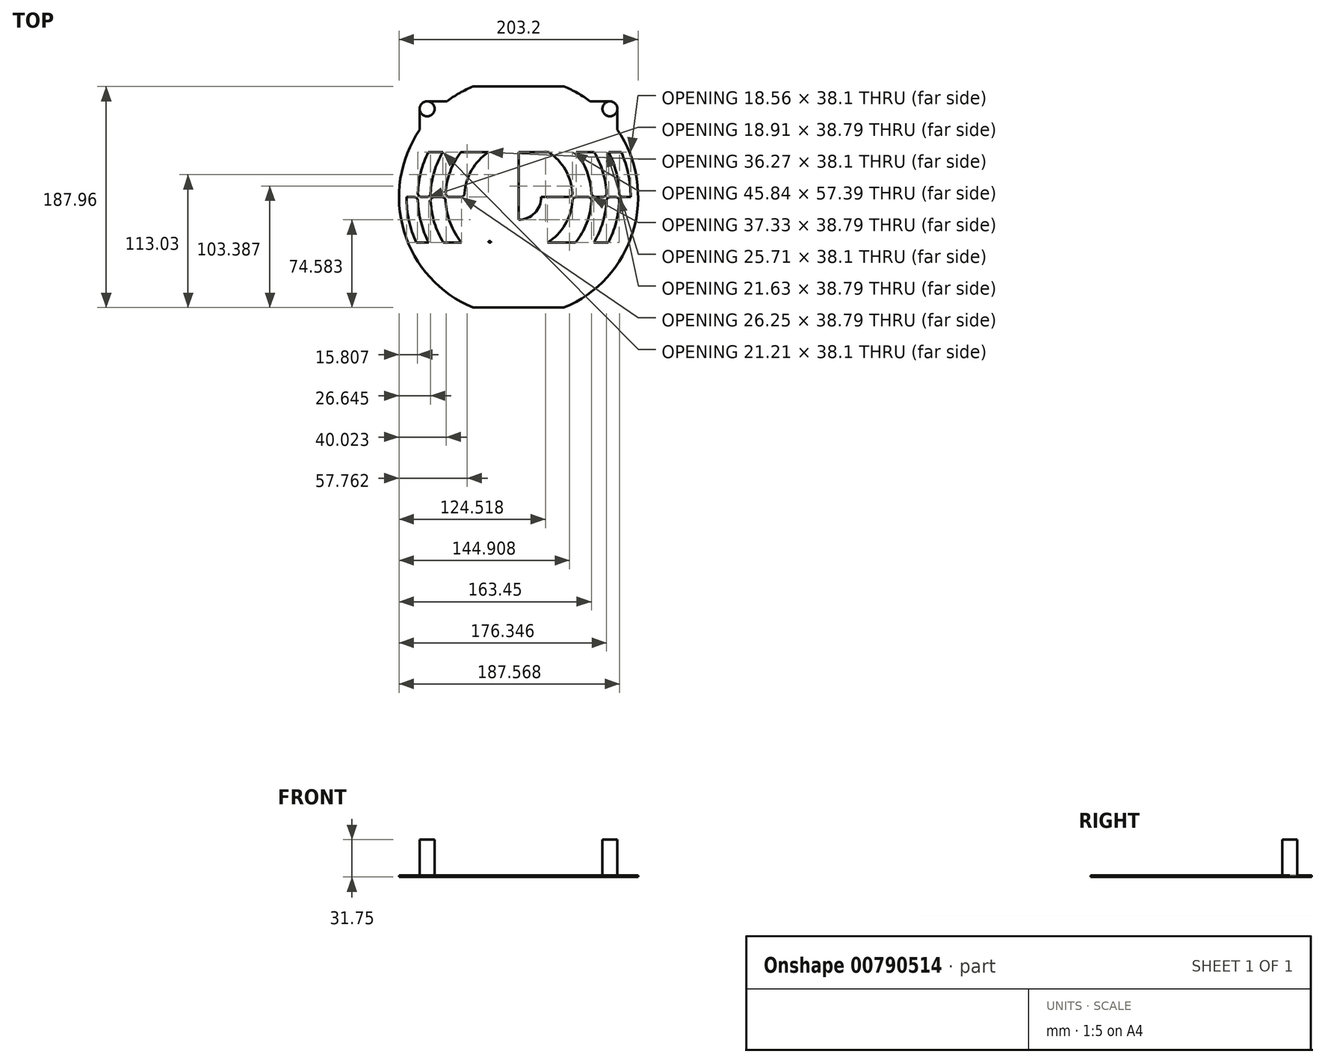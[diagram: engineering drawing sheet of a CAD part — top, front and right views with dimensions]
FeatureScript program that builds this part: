
annotation { "Feature Type Name" : "Feature", "Feature Type Description" : "" }
export const myFeature = defineFeature(function(context is Context, id is Id, definition is map)
    precondition{}
    {
        {
            var Q0;
            Q0=qCreatedBy(makeId("Top.planeOp"),FACE);
            var sketch = newSketch(context, id + "F0", { "sketchPlane" : qUnion([Q0])});
            skCircle(sketch, "E0", {"center": v(0, 0) * mm, "radius": 101.6 * mm});
            skCircle(sketch, "E1", {"center": v(0, 0) * mm, "radius": 45.96 * mm});
            skCircle(sketch, "E2", {"center": v(0, 0) * mm, "radius": 62.07 * mm});
            skCircle(sketch, "E3", {"center": v(0, 0) * mm, "radius": 74.78 * mm});
            skCircle(sketch, "E4", {"center": v(0, 0) * mm, "radius": 85.63 * mm});
            skLineSegment(sketch, "E5", {"start": v(0, 0) * mm, "end": v(0, 38.1) * mm, "construction": true});
            skLineSegment(sketch, "E6", {"start": v(0, 38.1) * mm, "end": v(123.54, 38.1) * mm});
            skLineSegment(sketch, "E7", {"start": v(123.54, 38.1) * mm, "end": v(123.54, 0) * mm});
            skLineSegment(sketch, "E8", {"start": v(123.54, 0) * mm, "end": v(-129.33, 0) * mm});
            skLineSegment(sketch, "E9", {"start": v(-129.33, 0) * mm, "end": v(-129.33, 38.1) * mm});
            skLineSegment(sketch, "E10", {"start": v(-129.33, 38.1) * mm, "end": v(0, 38.1) * mm});
            skLineSegment(sketch, "E11", {"start": v(-129.33, 0) * mm, "end": v(-129.33, -38.8) * mm});
            skLineSegment(sketch, "E12", {"start": v(-129.33, -38.8) * mm, "end": v(123.54, -38.8) * mm});
            skLineSegment(sketch, "E13", {"start": v(123.54, -38.8) * mm, "end": v(123.54, 0) * mm});
            skLineSegment(sketch, "E14", {"start": v(0, 38.1) * mm, "end": v(0, -38.8) * mm});
            skCircle(sketch, "E15", {"center": v(-24.64, -38.8) * mm, "radius": 1.27 * mm});
            skCircle(sketch, "E16", {"center": v(-48.45, -38.8) * mm, "radius": 1.27 * mm});
            skCircle(sketch, "E17", {"center": v(-63.93, -38.8) * mm, "radius": 1.27 * mm});
            skCircle(sketch, "E18", {"center": v(-76.34, -38.8) * mm, "radius": 1.27 * mm});
            skCircle(sketch, "E19", {"center": v(-76.69, 38.1) * mm, "radius": 1.27 * mm});
            skCircle(sketch, "E20", {"center": v(-63.93, 38.1) * mm, "radius": 1.27 * mm});
            skCircle(sketch, "E21", {"center": v(-49, 38.1) * mm, "radius": 1.27 * mm});
            skCircle(sketch, "E22", {"center": v(-25.7, 38.1) * mm, "radius": 1.27 * mm});
            skCircle(sketch, "E23", {"center": v(25.7, 38.1) * mm, "radius": 1.27 * mm});
            skCircle(sketch, "E24", {"center": v(49, 38.1) * mm, "radius": 1.27 * mm});
            skCircle(sketch, "E25", {"center": v(64.35, 38.1) * mm, "radius": 1.27 * mm});
            skCircle(sketch, "E26", {"center": v(76.69, 38.1) * mm, "radius": 1.27 * mm});
            skCircle(sketch, "E27", {"center": v(76.34, -38.8) * mm, "radius": 1.27 * mm});
            skCircle(sketch, "E28", {"center": v(63.93, -38.8) * mm, "radius": 1.27 * mm});
            skCircle(sketch, "E29", {"center": v(48.45, -38.8) * mm, "radius": 1.27 * mm});
            skCircle(sketch, "E30", {"center": v(24.64, -38.8) * mm, "radius": 1.27 * mm});
            skCircle(sketch, "E31", {"center": v(85.63, 0) * mm, "radius": 1.27 * mm});
            skCircle(sketch, "E32", {"center": v(74.78, 0) * mm, "radius": 1.27 * mm});
            skCircle(sketch, "E33", {"center": v(62.07, 0) * mm, "radius": 1.27 * mm});
            skCircle(sketch, "E34", {"center": v(45.96, 0) * mm, "radius": 1.27 * mm});
            skCircle(sketch, "E35", {"center": v(-45.96, 0) * mm, "radius": 1.27 * mm});
            skCircle(sketch, "E36", {"center": v(-62.07, 0) * mm, "radius": 1.27 * mm});
            skCircle(sketch, "E37", {"center": v(-74.78, 0) * mm, "radius": 1.27 * mm});
            skCircle(sketch, "E38", {"center": v(-85.63, 0) * mm, "radius": 1.27 * mm});
            skCircle(sketch, "E39", {"center": v(0, 0) * mm, "radius": 19.29 * mm});
            skCircle(sketch, "E40", {"center": v(-77.66, 74.98) * mm, "radius": 6.35 * mm});
            skCircle(sketch, "E41", {"center": v(77.66, 74.98) * mm, "radius": 6.35 * mm});
            skLineSegment(sketch, "E42", {"start": v(77.66, 74.98) * mm, "end": v(77.66, 81.33) * mm, "construction": true});
            skLineSegment(sketch, "E43", {"start": v(77.66, 74.98) * mm, "end": v(84, 74.98) * mm, "construction": true});
            skLineSegment(sketch, "E44", {"start": v(-77.66, 74.98) * mm, "end": v(-77.66, 81.33) * mm, "construction": true});
            skLineSegment(sketch, "E45", {"start": v(-77.66, 74.98) * mm, "end": v(-84, 74.98) * mm, "construction": true});
            skLineSegment(sketch, "E46", {"start": v(77.66, 81.33) * mm, "end": v(60.9, 81.33) * mm});
            skLineSegment(sketch, "E47", {"start": v(84, 74.98) * mm, "end": v(84, 57.14) * mm});
            skLineSegment(sketch, "E48", {"start": v(-77.66, 81.33) * mm, "end": v(-60.9, 81.33) * mm});
            skLineSegment(sketch, "E49", {"start": v(-84, 74.98) * mm, "end": v(-84, 57.14) * mm});
            skSolve(sketch);
        }
        {
            var Q0;
            {var subQ3=sQuery(id+"F0.wireOp",EDGE,"E22");var subQ5=sQuery(id+"F0.wireOp",EDGE,"E1");var subQ6=makeQuery(id+"F0.imprint","INTERSECT",VERTEX,{"disambiguationData":[OD(1.0)],"derivedFrom":[subQ5,subQ3]});Q0=makeQuery(id+"F0.imprint","IMPRINT",FACE,{"disambiguationData":[TD([[makeQuery(id+"F0.imprint","IMPRINT",EDGE,{"disambiguationData":[TD([[subQ6,-1.0]])],"derivedFrom":subQ5}),1.0]])]});}
            var Q1;
            {var subQ3=sQuery(id+"F0.wireOp",EDGE,"E30");var subQ11=sQuery(id+"F0.wireOp",EDGE,"E1");var subQ12=makeQuery(id+"F0.imprint","INTERSECT",VERTEX,{"disambiguationData":[OD(1.0)],"derivedFrom":[subQ11,subQ3]});Q1=makeQuery(id+"F0.imprint","IMPRINT",FACE,{"disambiguationData":[TD([[makeQuery(id+"F0.imprint","IMPRINT",EDGE,{"disambiguationData":[TD([[subQ12,-1.0]])],"derivedFrom":subQ11}),1.0]])]});}
            var Q2;
            {var subQ3=sQuery(id+"F0.wireOp",EDGE,"E34");var subQ13=sQuery(id+"F0.wireOp",EDGE,"E1");var subQ14=makeQuery(id+"F0.imprint","INTERSECT",VERTEX,{"disambiguationData":[OD(0.0)],"derivedFrom":[subQ13,subQ3]});Q2=makeQuery(id+"F0.imprint","IMPRINT",FACE,{"disambiguationData":[TD([[makeQuery(id+"F0.imprint","IMPRINT",EDGE,{"disambiguationData":[TD([[subQ14,-1.0]])],"derivedFrom":subQ13}),-1.0]])]});}
            var Q3;
            {var subQ0=sQuery(id+"F0.wireOp",EDGE,"E29");var subQ8=sQuery(id+"F0.wireOp",EDGE,"E2");var subQ15=makeQuery(id+"F0.imprint","INTERSECT",VERTEX,{"disambiguationData":[OD(1.0)],"derivedFrom":[subQ8,subQ0]});Q3=makeQuery(id+"F0.imprint","IMPRINT",FACE,{"disambiguationData":[TD([[makeQuery(id+"F0.imprint","IMPRINT",EDGE,{"disambiguationData":[TD([[subQ15,-1.0]])],"derivedFrom":subQ8}),-1.0]])]});}
            var Q4;
            {var subQ3=sQuery(id+"F0.wireOp",EDGE,"E32");var subQ10=sQuery(id+"F0.wireOp",EDGE,"E3");var subQ11=makeQuery(id+"F0.imprint","INTERSECT",VERTEX,{"disambiguationData":[OD(0.0)],"derivedFrom":[subQ10,subQ3]});Q4=makeQuery(id+"F0.imprint","IMPRINT",FACE,{"disambiguationData":[TD([[makeQuery(id+"F0.imprint","IMPRINT",EDGE,{"disambiguationData":[TD([[subQ11,-1.0]])],"derivedFrom":subQ10}),-1.0]])]});}
            var Q5;
            {var subQ1=sQuery(id+"F0.wireOp",EDGE,"E0");var subQ9=sQuery(id+"F0.wireOp",EDGE,"E12");var subQ10=makeQuery(id+"F0.imprint","INTERSECT",VERTEX,{"disambiguationData":[OD(1.0)],"derivedFrom":[subQ1,subQ9]});Q5=makeQuery(id+"F0.imprint","IMPRINT",FACE,{"disambiguationData":[TD([[makeQuery(id+"F0.imprint","IMPRINT",EDGE,{"disambiguationData":[TD([[subQ10,-1.0]])],"derivedFrom":subQ1}),1.0]])]});}
            var Q6;
            {var subQ0=sQuery(id+"F0.wireOp",EDGE,"E35");var subQ13=sQuery(id+"F0.wireOp",EDGE,"E1");var subQ14=makeQuery(id+"F0.imprint","INTERSECT",VERTEX,{"disambiguationData":[OD(1.0)],"derivedFrom":[subQ13,subQ0]});Q6=makeQuery(id+"F0.imprint","IMPRINT",FACE,{"disambiguationData":[TD([[makeQuery(id+"F0.imprint","IMPRINT",EDGE,{"disambiguationData":[TD([[subQ14,-1.0]])],"derivedFrom":subQ13}),-1.0]])]});}
            var Q7;
            {var subQ11=sQuery(id+"F0.wireOp",EDGE,"E21");var subQ13=sQuery(id+"F0.wireOp",EDGE,"E2");var subQ14=makeQuery(id+"F0.imprint","INTERSECT",VERTEX,{"disambiguationData":[OD(1.0)],"derivedFrom":[subQ13,subQ11]});Q7=makeQuery(id+"F0.imprint","IMPRINT",FACE,{"disambiguationData":[TD([[makeQuery(id+"F0.imprint","IMPRINT",EDGE,{"disambiguationData":[TD([[subQ14,-1.0]])],"derivedFrom":subQ13}),-1.0]])]});}
            var Q8;
            {var subQ5=sQuery(id+"F0.wireOp",EDGE,"E37");var subQ10=sQuery(id+"F0.wireOp",EDGE,"E3");var subQ11=makeQuery(id+"F0.imprint","INTERSECT",VERTEX,{"disambiguationData":[OD(1.0)],"derivedFrom":[subQ10,subQ5]});Q8=makeQuery(id+"F0.imprint","IMPRINT",FACE,{"disambiguationData":[TD([[makeQuery(id+"F0.imprint","IMPRINT",EDGE,{"disambiguationData":[TD([[subQ11,-1.0]])],"derivedFrom":subQ10}),-1.0]])]});}
            var Q9;
            {var subQ0=sQuery(id+"F0.wireOp",EDGE,"E10");var subQ1=sQuery(id+"F0.wireOp",EDGE,"E0");var subQ2=makeQuery(id+"F0.imprint","INTERSECT",VERTEX,{"derivedFrom":[subQ1,subQ0]});Q9=makeQuery(id+"F0.imprint","IMPRINT",FACE,{"disambiguationData":[TD([[makeQuery(id+"F0.imprint","IMPRINT",EDGE,{"disambiguationData":[TD([[subQ2,-1.0]])],"derivedFrom":subQ1}),1.0]])]});}
            var Q10;
            {var subQ0=sQuery(id+"F0.wireOp",EDGE,"E38");var subQ1=sQuery(id+"F0.wireOp",EDGE,"E4");var subQ2=makeQuery(id+"F0.imprint","INTERSECT",VERTEX,{"disambiguationData":[OD(0.0)],"derivedFrom":[subQ1,subQ0]});Q10=makeQuery(id+"F0.imprint","IMPRINT",FACE,{"disambiguationData":[TD([[makeQuery(id+"F0.imprint","IMPRINT",EDGE,{"disambiguationData":[TD([[subQ2,-1.0]])],"derivedFrom":subQ1}),1.0]])]});}
            var Q11;
            {var subQ0=sQuery(id+"F0.wireOp",EDGE,"E8");var subQ1=sQuery(id+"F0.wireOp",EDGE,"E4");var subQ2=makeQuery(id+"F0.imprint","INTERSECT",VERTEX,{"disambiguationData":[OD(1.0)],"derivedFrom":[subQ1,subQ0]});Q11=makeQuery(id+"F0.imprint","IMPRINT",FACE,{"disambiguationData":[TD([[makeQuery(id+"F0.imprint","IMPRINT",EDGE,{"disambiguationData":[TD([[subQ2,-1.0]])],"derivedFrom":subQ1}),1.0]])]});}
            var Q12;
            {var subQ0=sQuery(id+"F0.wireOp",EDGE,"E8");var subQ1=sQuery(id+"F0.wireOp",EDGE,"E4");var subQ2=makeQuery(id+"F0.imprint","INTERSECT",VERTEX,{"disambiguationData":[OD(1.0)],"derivedFrom":[subQ1,subQ0]});Q12=makeQuery(id+"F0.imprint","IMPRINT",FACE,{"disambiguationData":[TD([[makeQuery(id+"F0.imprint","IMPRINT",EDGE,{"disambiguationData":[TD([[subQ2,-1.0]])],"derivedFrom":subQ1}),-1.0]])]});}
            var Q13;
            {var subQ0=sQuery(id+"F0.wireOp",EDGE,"E38");var subQ1=sQuery(id+"F0.wireOp",EDGE,"E4");var subQ2=makeQuery(id+"F0.imprint","INTERSECT",VERTEX,{"disambiguationData":[OD(0.0)],"derivedFrom":[subQ1,subQ0]});Q13=makeQuery(id+"F0.imprint","IMPRINT",FACE,{"disambiguationData":[TD([[makeQuery(id+"F0.imprint","IMPRINT",EDGE,{"disambiguationData":[TD([[subQ2,-1.0]])],"derivedFrom":subQ1}),-1.0]])]});}
            var Q14;
            {var subQ0=sQuery(id+"F0.wireOp",EDGE,"E37");var subQ1=sQuery(id+"F0.wireOp",EDGE,"E3");var subQ2=makeQuery(id+"F0.imprint","INTERSECT",VERTEX,{"disambiguationData":[OD(0.0)],"derivedFrom":[subQ1,subQ0]});Q14=makeQuery(id+"F0.imprint","IMPRINT",FACE,{"disambiguationData":[TD([[makeQuery(id+"F0.imprint","IMPRINT",EDGE,{"disambiguationData":[TD([[subQ2,-1.0]])],"derivedFrom":subQ1}),-1.0]])]});}
            var Q15;
            {var subQ0=sQuery(id+"F0.wireOp",EDGE,"E37");var subQ1=sQuery(id+"F0.wireOp",EDGE,"E3");var subQ2=makeQuery(id+"F0.imprint","INTERSECT",VERTEX,{"disambiguationData":[OD(0.0)],"derivedFrom":[subQ1,subQ0]});Q15=makeQuery(id+"F0.imprint","IMPRINT",FACE,{"disambiguationData":[TD([[makeQuery(id+"F0.imprint","IMPRINT",EDGE,{"disambiguationData":[TD([[subQ2,-1.0]])],"derivedFrom":subQ1}),1.0]])]});}
            var Q16;
            {var subQ0=sQuery(id+"F0.wireOp",EDGE,"E8");var subQ1=sQuery(id+"F0.wireOp",EDGE,"E3");var subQ2=makeQuery(id+"F0.imprint","INTERSECT",VERTEX,{"disambiguationData":[OD(1.0)],"derivedFrom":[subQ1,subQ0]});Q16=makeQuery(id+"F0.imprint","IMPRINT",FACE,{"disambiguationData":[TD([[makeQuery(id+"F0.imprint","IMPRINT",EDGE,{"disambiguationData":[TD([[subQ2,-1.0]])],"derivedFrom":subQ1}),1.0]])]});}
            var Q17;
            {var subQ0=sQuery(id+"F0.wireOp",EDGE,"E8");var subQ1=sQuery(id+"F0.wireOp",EDGE,"E3");var subQ2=makeQuery(id+"F0.imprint","INTERSECT",VERTEX,{"disambiguationData":[OD(1.0)],"derivedFrom":[subQ1,subQ0]});Q17=makeQuery(id+"F0.imprint","IMPRINT",FACE,{"disambiguationData":[TD([[makeQuery(id+"F0.imprint","IMPRINT",EDGE,{"disambiguationData":[TD([[subQ2,-1.0]])],"derivedFrom":subQ1}),-1.0]])]});}
            var Q18;
            {var subQ0=sQuery(id+"F0.wireOp",EDGE,"E36");var subQ1=sQuery(id+"F0.wireOp",EDGE,"E2");var subQ2=makeQuery(id+"F0.imprint","INTERSECT",VERTEX,{"disambiguationData":[OD(0.0)],"derivedFrom":[subQ1,subQ0]});Q18=makeQuery(id+"F0.imprint","IMPRINT",FACE,{"disambiguationData":[TD([[makeQuery(id+"F0.imprint","IMPRINT",EDGE,{"disambiguationData":[TD([[subQ2,-1.0]])],"derivedFrom":subQ1}),-1.0]])]});}
            var Q19;
            {var subQ0=sQuery(id+"F0.wireOp",EDGE,"E36");var subQ1=sQuery(id+"F0.wireOp",EDGE,"E2");var subQ2=makeQuery(id+"F0.imprint","INTERSECT",VERTEX,{"disambiguationData":[OD(0.0)],"derivedFrom":[subQ1,subQ0]});Q19=makeQuery(id+"F0.imprint","IMPRINT",FACE,{"disambiguationData":[TD([[makeQuery(id+"F0.imprint","IMPRINT",EDGE,{"disambiguationData":[TD([[subQ2,-1.0]])],"derivedFrom":subQ1}),1.0]])]});}
            var Q20;
            {var subQ0=sQuery(id+"F0.wireOp",EDGE,"E8");var subQ1=sQuery(id+"F0.wireOp",EDGE,"E2");var subQ2=makeQuery(id+"F0.imprint","INTERSECT",VERTEX,{"disambiguationData":[OD(1.0)],"derivedFrom":[subQ1,subQ0]});Q20=makeQuery(id+"F0.imprint","IMPRINT",FACE,{"disambiguationData":[TD([[makeQuery(id+"F0.imprint","IMPRINT",EDGE,{"disambiguationData":[TD([[subQ2,-1.0]])],"derivedFrom":subQ1}),1.0]])]});}
            var Q21;
            {var subQ0=sQuery(id+"F0.wireOp",EDGE,"E8");var subQ1=sQuery(id+"F0.wireOp",EDGE,"E2");var subQ2=makeQuery(id+"F0.imprint","INTERSECT",VERTEX,{"disambiguationData":[OD(1.0)],"derivedFrom":[subQ1,subQ0]});Q21=makeQuery(id+"F0.imprint","IMPRINT",FACE,{"disambiguationData":[TD([[makeQuery(id+"F0.imprint","IMPRINT",EDGE,{"disambiguationData":[TD([[subQ2,-1.0]])],"derivedFrom":subQ1}),-1.0]])]});}
            var Q22;
            {var subQ0=sQuery(id+"F0.wireOp",EDGE,"E35");var subQ1=sQuery(id+"F0.wireOp",EDGE,"E1");var subQ2=makeQuery(id+"F0.imprint","INTERSECT",VERTEX,{"disambiguationData":[OD(0.0)],"derivedFrom":[subQ1,subQ0]});Q22=makeQuery(id+"F0.imprint","IMPRINT",FACE,{"disambiguationData":[TD([[makeQuery(id+"F0.imprint","IMPRINT",EDGE,{"disambiguationData":[TD([[subQ2,-1.0]])],"derivedFrom":subQ1}),-1.0]])]});}
            var Q23;
            {var subQ0=sQuery(id+"F0.wireOp",EDGE,"E35");var subQ1=sQuery(id+"F0.wireOp",EDGE,"E1");var subQ2=makeQuery(id+"F0.imprint","INTERSECT",VERTEX,{"disambiguationData":[OD(0.0)],"derivedFrom":[subQ1,subQ0]});Q23=makeQuery(id+"F0.imprint","IMPRINT",FACE,{"disambiguationData":[TD([[makeQuery(id+"F0.imprint","IMPRINT",EDGE,{"disambiguationData":[TD([[subQ2,-1.0]])],"derivedFrom":subQ1}),1.0]])]});}
            var Q24;
            {var subQ0=sQuery(id+"F0.wireOp",EDGE,"E8");var subQ1=sQuery(id+"F0.wireOp",EDGE,"E1");var subQ2=makeQuery(id+"F0.imprint","INTERSECT",VERTEX,{"disambiguationData":[OD(1.0)],"derivedFrom":[subQ1,subQ0]});Q24=makeQuery(id+"F0.imprint","IMPRINT",FACE,{"disambiguationData":[TD([[makeQuery(id+"F0.imprint","IMPRINT",EDGE,{"disambiguationData":[TD([[subQ2,-1.0]])],"derivedFrom":subQ1}),1.0]])]});}
            var Q25;
            {var subQ0=sQuery(id+"F0.wireOp",EDGE,"E8");var subQ1=sQuery(id+"F0.wireOp",EDGE,"E1");var subQ2=makeQuery(id+"F0.imprint","INTERSECT",VERTEX,{"disambiguationData":[OD(1.0)],"derivedFrom":[subQ1,subQ0]});Q25=makeQuery(id+"F0.imprint","IMPRINT",FACE,{"disambiguationData":[TD([[makeQuery(id+"F0.imprint","IMPRINT",EDGE,{"disambiguationData":[TD([[subQ2,-1.0]])],"derivedFrom":subQ1}),-1.0]])]});}
            var Q26;
            {var subQ0=sQuery(id+"F0.wireOp",EDGE,"E8");var subQ1=sQuery(id+"F0.wireOp",EDGE,"E1");var subQ2=makeQuery(id+"F0.imprint","INTERSECT",VERTEX,{"disambiguationData":[OD(0.0)],"derivedFrom":[subQ1,subQ0]});Q26=makeQuery(id+"F0.imprint","IMPRINT",FACE,{"disambiguationData":[TD([[makeQuery(id+"F0.imprint","IMPRINT",EDGE,{"disambiguationData":[TD([[subQ2,1.0]])],"derivedFrom":subQ1}),-1.0]])]});}
            var Q27;
            {var subQ0=sQuery(id+"F0.wireOp",EDGE,"E34");var subQ1=sQuery(id+"F0.wireOp",EDGE,"E1");var subQ2=makeQuery(id+"F0.imprint","INTERSECT",VERTEX,{"disambiguationData":[OD(0.0)],"derivedFrom":[subQ1,subQ0]});Q27=makeQuery(id+"F0.imprint","IMPRINT",FACE,{"disambiguationData":[TD([[makeQuery(id+"F0.imprint","IMPRINT",EDGE,{"disambiguationData":[TD([[subQ2,1.0]])],"derivedFrom":subQ1}),-1.0]])]});}
            var Q28;
            {var subQ0=sQuery(id+"F0.wireOp",EDGE,"E34");var subQ1=sQuery(id+"F0.wireOp",EDGE,"E1");var subQ2=makeQuery(id+"F0.imprint","INTERSECT",VERTEX,{"disambiguationData":[OD(0.0)],"derivedFrom":[subQ1,subQ0]});Q28=makeQuery(id+"F0.imprint","IMPRINT",FACE,{"disambiguationData":[TD([[makeQuery(id+"F0.imprint","IMPRINT",EDGE,{"disambiguationData":[TD([[subQ2,1.0]])],"derivedFrom":subQ1}),1.0]])]});}
            var Q29;
            {var subQ0=sQuery(id+"F0.wireOp",EDGE,"E33");var subQ1=sQuery(id+"F0.wireOp",EDGE,"E2");var subQ2=makeQuery(id+"F0.imprint","INTERSECT",VERTEX,{"disambiguationData":[OD(0.0)],"derivedFrom":[subQ1,subQ0]});Q29=makeQuery(id+"F0.imprint","IMPRINT",FACE,{"disambiguationData":[TD([[makeQuery(id+"F0.imprint","IMPRINT",EDGE,{"disambiguationData":[TD([[subQ2,1.0]])],"derivedFrom":subQ1}),1.0]])]});}
            var Q30;
            {var subQ0=sQuery(id+"F0.wireOp",EDGE,"E33");var subQ1=sQuery(id+"F0.wireOp",EDGE,"E2");var subQ2=makeQuery(id+"F0.imprint","INTERSECT",VERTEX,{"disambiguationData":[OD(0.0)],"derivedFrom":[subQ1,subQ0]});Q30=makeQuery(id+"F0.imprint","IMPRINT",FACE,{"disambiguationData":[TD([[makeQuery(id+"F0.imprint","IMPRINT",EDGE,{"disambiguationData":[TD([[subQ2,1.0]])],"derivedFrom":subQ1}),-1.0]])]});}
            var Q31;
            {var subQ0=sQuery(id+"F0.wireOp",EDGE,"E8");var subQ1=sQuery(id+"F0.wireOp",EDGE,"E2");var subQ2=makeQuery(id+"F0.imprint","INTERSECT",VERTEX,{"disambiguationData":[OD(0.0)],"derivedFrom":[subQ1,subQ0]});Q31=makeQuery(id+"F0.imprint","IMPRINT",FACE,{"disambiguationData":[TD([[makeQuery(id+"F0.imprint","IMPRINT",EDGE,{"disambiguationData":[TD([[subQ2,1.0]])],"derivedFrom":subQ1}),-1.0]])]});}
            var Q32;
            {var subQ0=sQuery(id+"F0.wireOp",EDGE,"E8");var subQ1=sQuery(id+"F0.wireOp",EDGE,"E2");var subQ2=makeQuery(id+"F0.imprint","INTERSECT",VERTEX,{"disambiguationData":[OD(0.0)],"derivedFrom":[subQ1,subQ0]});Q32=makeQuery(id+"F0.imprint","IMPRINT",FACE,{"disambiguationData":[TD([[makeQuery(id+"F0.imprint","IMPRINT",EDGE,{"disambiguationData":[TD([[subQ2,1.0]])],"derivedFrom":subQ1}),1.0]])]});}
            var Q33;
            {var subQ0=sQuery(id+"F0.wireOp",EDGE,"E32");var subQ1=sQuery(id+"F0.wireOp",EDGE,"E3");var subQ2=makeQuery(id+"F0.imprint","INTERSECT",VERTEX,{"disambiguationData":[OD(0.0)],"derivedFrom":[subQ1,subQ0]});Q33=makeQuery(id+"F0.imprint","IMPRINT",FACE,{"disambiguationData":[TD([[makeQuery(id+"F0.imprint","IMPRINT",EDGE,{"disambiguationData":[TD([[subQ2,1.0]])],"derivedFrom":subQ1}),1.0]])]});}
            var Q34;
            {var subQ0=sQuery(id+"F0.wireOp",EDGE,"E8");var subQ1=sQuery(id+"F0.wireOp",EDGE,"E3");var subQ2=makeQuery(id+"F0.imprint","INTERSECT",VERTEX,{"disambiguationData":[OD(0.0)],"derivedFrom":[subQ1,subQ0]});Q34=makeQuery(id+"F0.imprint","IMPRINT",FACE,{"disambiguationData":[TD([[makeQuery(id+"F0.imprint","IMPRINT",EDGE,{"disambiguationData":[TD([[subQ2,1.0]])],"derivedFrom":subQ1}),1.0]])]});}
            var Q35;
            {var subQ0=sQuery(id+"F0.wireOp",EDGE,"E8");var subQ1=sQuery(id+"F0.wireOp",EDGE,"E3");var subQ2=makeQuery(id+"F0.imprint","INTERSECT",VERTEX,{"disambiguationData":[OD(0.0)],"derivedFrom":[subQ1,subQ0]});Q35=makeQuery(id+"F0.imprint","IMPRINT",FACE,{"disambiguationData":[TD([[makeQuery(id+"F0.imprint","IMPRINT",EDGE,{"disambiguationData":[TD([[subQ2,1.0]])],"derivedFrom":subQ1}),-1.0]])]});}
            var Q36;
            {var subQ0=sQuery(id+"F0.wireOp",EDGE,"E32");var subQ1=sQuery(id+"F0.wireOp",EDGE,"E3");var subQ2=makeQuery(id+"F0.imprint","INTERSECT",VERTEX,{"disambiguationData":[OD(0.0)],"derivedFrom":[subQ1,subQ0]});Q36=makeQuery(id+"F0.imprint","IMPRINT",FACE,{"disambiguationData":[TD([[makeQuery(id+"F0.imprint","IMPRINT",EDGE,{"disambiguationData":[TD([[subQ2,1.0]])],"derivedFrom":subQ1}),-1.0]])]});}
            var Q37;
            {var subQ0=sQuery(id+"F0.wireOp",EDGE,"E31");var subQ1=sQuery(id+"F0.wireOp",EDGE,"E4");var subQ2=makeQuery(id+"F0.imprint","INTERSECT",VERTEX,{"disambiguationData":[OD(0.0)],"derivedFrom":[subQ1,subQ0]});Q37=makeQuery(id+"F0.imprint","IMPRINT",FACE,{"disambiguationData":[TD([[makeQuery(id+"F0.imprint","IMPRINT",EDGE,{"disambiguationData":[TD([[subQ2,1.0]])],"derivedFrom":subQ1}),1.0]])]});}
            var Q38;
            {var subQ0=sQuery(id+"F0.wireOp",EDGE,"E31");var subQ1=sQuery(id+"F0.wireOp",EDGE,"E4");var subQ2=makeQuery(id+"F0.imprint","INTERSECT",VERTEX,{"disambiguationData":[OD(0.0)],"derivedFrom":[subQ1,subQ0]});Q38=makeQuery(id+"F0.imprint","IMPRINT",FACE,{"disambiguationData":[TD([[makeQuery(id+"F0.imprint","IMPRINT",EDGE,{"disambiguationData":[TD([[subQ2,1.0]])],"derivedFrom":subQ1}),-1.0]])]});}
            var Q39;
            {var subQ0=sQuery(id+"F0.wireOp",EDGE,"E8");var subQ1=sQuery(id+"F0.wireOp",EDGE,"E4");var subQ2=makeQuery(id+"F0.imprint","INTERSECT",VERTEX,{"disambiguationData":[OD(0.0)],"derivedFrom":[subQ1,subQ0]});Q39=makeQuery(id+"F0.imprint","IMPRINT",FACE,{"disambiguationData":[TD([[makeQuery(id+"F0.imprint","IMPRINT",EDGE,{"disambiguationData":[TD([[subQ2,1.0]])],"derivedFrom":subQ1}),-1.0]])]});}
            var Q40;
            {var subQ0=sQuery(id+"F0.wireOp",EDGE,"E8");var subQ1=sQuery(id+"F0.wireOp",EDGE,"E4");var subQ2=makeQuery(id+"F0.imprint","INTERSECT",VERTEX,{"disambiguationData":[OD(0.0)],"derivedFrom":[subQ1,subQ0]});Q40=makeQuery(id+"F0.imprint","IMPRINT",FACE,{"disambiguationData":[TD([[makeQuery(id+"F0.imprint","IMPRINT",EDGE,{"disambiguationData":[TD([[subQ2,1.0]])],"derivedFrom":subQ1}),1.0]])]});}
            var Q41;
            {var subQ0=sQuery(id+"F0.wireOp",EDGE,"E14");var subQ1=sQuery(id+"F0.wireOp",EDGE,"E8");var subQ2=makeQuery(id+"F0.imprint","INTERSECT",VERTEX,{"derivedFrom":[subQ1,subQ0]});Q41=makeQuery(id+"F0.imprint","IMPRINT",FACE,{"disambiguationData":[TD([[makeQuery(id+"F0.imprint","IMPRINT",EDGE,{"disambiguationData":[TD([[subQ2,-1.0]])],"derivedFrom":subQ1}),-1.0]])]});}
            var Q42;
            {var subQ0=sQuery(id+"F0.wireOp",EDGE,"E39");var subQ1=sQuery(id+"F0.wireOp",EDGE,"E8");var subQ2=makeQuery(id+"F0.imprint","INTERSECT",VERTEX,{"disambiguationData":[OD(0.0)],"derivedFrom":[subQ1,subQ0]});Q42=makeQuery(id+"F0.imprint","IMPRINT",FACE,{"disambiguationData":[TD([[makeQuery(id+"F0.imprint","IMPRINT",EDGE,{"disambiguationData":[TD([[subQ2,-1.0]])],"derivedFrom":subQ1}),-1.0]])]});}
            var Q43;
            {var subQ0=sQuery(id+"F0.wireOp",EDGE,"E39");var subQ1=sQuery(id+"F0.wireOp",EDGE,"E8");var subQ2=makeQuery(id+"F0.imprint","INTERSECT",VERTEX,{"disambiguationData":[OD(0.0)],"derivedFrom":[subQ1,subQ0]});Q43=makeQuery(id+"F0.imprint","IMPRINT",FACE,{"disambiguationData":[TD([[makeQuery(id+"F0.imprint","IMPRINT",EDGE,{"disambiguationData":[TD([[subQ2,-1.0]])],"derivedFrom":subQ1}),1.0]])]});}
            var Q44;
            {var subQ0=sQuery(id+"F0.wireOp",EDGE,"E14");var subQ1=sQuery(id+"F0.wireOp",EDGE,"E8");var subQ2=makeQuery(id+"F0.imprint","INTERSECT",VERTEX,{"derivedFrom":[subQ1,subQ0]});Q44=makeQuery(id+"F0.imprint","IMPRINT",FACE,{"disambiguationData":[TD([[makeQuery(id+"F0.imprint","IMPRINT",EDGE,{"disambiguationData":[TD([[subQ2,-1.0]])],"derivedFrom":subQ1}),1.0]])]});}
            var Q45;
            {var subQ0=sQuery(id+"F0.wireOp",EDGE,"E8");var subQ1=sQuery(id+"F0.wireOp",EDGE,"E1");var subQ2=makeQuery(id+"F0.imprint","INTERSECT",VERTEX,{"disambiguationData":[OD(0.0)],"derivedFrom":[subQ1,subQ0]});Q45=makeQuery(id+"F0.imprint","IMPRINT",FACE,{"disambiguationData":[TD([[makeQuery(id+"F0.imprint","IMPRINT",EDGE,{"disambiguationData":[TD([[subQ2,1.0]])],"derivedFrom":subQ1}),1.0]])]});}
            var Q46;
            {var subQ1=sQuery(id+"F0.wireOp",EDGE,"E0");var subQ5=sQuery(id+"F0.wireOp",EDGE,"E6");var subQ6=makeQuery(id+"F0.imprint","INTERSECT",VERTEX,{"derivedFrom":[subQ1,subQ5]});Q46=makeQuery(id+"F0.imprint","IMPRINT",FACE,{"disambiguationData":[TD([[makeQuery(id+"F0.imprint","IMPRINT",EDGE,{"disambiguationData":[TD([[subQ6,-1.0]])],"derivedFrom":subQ1}),1.0]])]});}
            var Q47;
            {var subQ5=sQuery(id+"F0.wireOp",EDGE,"E25");var subQ13=sQuery(id+"F0.wireOp",EDGE,"E3");var subQ14=makeQuery(id+"F0.imprint","INTERSECT",VERTEX,{"disambiguationData":[OD(1.0)],"derivedFrom":[subQ13,subQ5]});Q47=makeQuery(id+"F0.imprint","IMPRINT",FACE,{"disambiguationData":[TD([[makeQuery(id+"F0.imprint","IMPRINT",EDGE,{"disambiguationData":[TD([[subQ14,-1.0]])],"derivedFrom":subQ13}),-1.0]])]});}
            var Q48;
            {var subQ0=sQuery(id+"F0.wireOp",EDGE,"E24");var subQ10=sQuery(id+"F0.wireOp",EDGE,"E2");var subQ12=makeQuery(id+"F0.imprint","INTERSECT",VERTEX,{"disambiguationData":[OD(1.0)],"derivedFrom":[subQ10,subQ0]});Q48=makeQuery(id+"F0.imprint","IMPRINT",FACE,{"disambiguationData":[TD([[makeQuery(id+"F0.imprint","IMPRINT",EDGE,{"disambiguationData":[TD([[subQ12,-1.0]])],"derivedFrom":subQ10}),-1.0]])]});}
            var Q49;
            {var subQ5=sQuery(id+"F0.wireOp",EDGE,"E23");var subQ13=sQuery(id+"F0.wireOp",EDGE,"E1");var subQ14=makeQuery(id+"F0.imprint","INTERSECT",VERTEX,{"disambiguationData":[OD(1.0)],"derivedFrom":[subQ13,subQ5]});Q49=makeQuery(id+"F0.imprint","IMPRINT",FACE,{"disambiguationData":[TD([[makeQuery(id+"F0.imprint","IMPRINT",EDGE,{"disambiguationData":[TD([[subQ14,-1.0]])],"derivedFrom":subQ13}),-1.0]])]});}
            var Q50;
            {var subQ5=sQuery(id+"F0.wireOp",EDGE,"E23");var subQ7=sQuery(id+"F0.wireOp",EDGE,"E1");var subQ9=makeQuery(id+"F0.imprint","INTERSECT",VERTEX,{"disambiguationData":[OD(1.0)],"derivedFrom":[subQ7,subQ5]});Q50=makeQuery(id+"F0.imprint","IMPRINT",FACE,{"disambiguationData":[TD([[makeQuery(id+"F0.imprint","IMPRINT",EDGE,{"disambiguationData":[TD([[subQ9,-1.0]])],"derivedFrom":subQ7}),1.0]])]});}
            var Q51;
            {var subQ0=sQuery(id+"F0.wireOp",EDGE,"E15");var subQ1=sQuery(id+"F0.wireOp",EDGE,"E1");var subQ2=makeQuery(id+"F0.imprint","INTERSECT",VERTEX,{"disambiguationData":[OD(1.0)],"derivedFrom":[subQ1,subQ0]});Q51=makeQuery(id+"F0.imprint","IMPRINT",FACE,{"disambiguationData":[TD([[makeQuery(id+"F0.imprint","IMPRINT",EDGE,{"disambiguationData":[TD([[subQ2,-1.0]])],"derivedFrom":subQ1}),1.0]])]});}
            var Q52;
            {var subQ7=sQuery(id+"F0.wireOp",EDGE,"E16");var subQ12=sQuery(id+"F0.wireOp",EDGE,"E2");var subQ14=makeQuery(id+"F0.imprint","INTERSECT",VERTEX,{"disambiguationData":[OD(1.0)],"derivedFrom":[subQ12,subQ7]});Q52=makeQuery(id+"F0.imprint","IMPRINT",FACE,{"disambiguationData":[TD([[makeQuery(id+"F0.imprint","IMPRINT",EDGE,{"disambiguationData":[TD([[subQ14,-1.0]])],"derivedFrom":subQ12}),-1.0]])]});}
            var Q53;
            {var subQ7=sQuery(id+"F0.wireOp",EDGE,"E17");var subQ9=sQuery(id+"F0.wireOp",EDGE,"E3");var subQ10=makeQuery(id+"F0.imprint","INTERSECT",VERTEX,{"disambiguationData":[OD(1.0)],"derivedFrom":[subQ9,subQ7]});Q53=makeQuery(id+"F0.imprint","IMPRINT",FACE,{"disambiguationData":[TD([[makeQuery(id+"F0.imprint","IMPRINT",EDGE,{"disambiguationData":[TD([[subQ10,-1.0]])],"derivedFrom":subQ9}),-1.0]])]});}
            var Q54;
            {var subQ0=sQuery(id+"F0.wireOp",EDGE,"E12");var subQ1=sQuery(id+"F0.wireOp",EDGE,"E0");var subQ5=makeQuery(id+"F0.imprint","INTERSECT",VERTEX,{"disambiguationData":[OD(0.0)],"derivedFrom":[subQ1,subQ0]});Q54=makeQuery(id+"F0.imprint","IMPRINT",FACE,{"disambiguationData":[TD([[makeQuery(id+"F0.imprint","IMPRINT",EDGE,{"disambiguationData":[TD([[subQ5,-1.0]])],"derivedFrom":subQ1}),1.0]])]});}
            var Q55;
            {var subQ0=sQuery(id+"F0.wireOp",EDGE,"E23");var subQ1=sQuery(id+"F0.wireOp",EDGE,"E1");var subQ2=makeQuery(id+"F0.imprint","INTERSECT",VERTEX,{"disambiguationData":[OD(0.0)],"derivedFrom":[subQ1,subQ0]});Q55=makeQuery(id+"F0.imprint","IMPRINT",FACE,{"disambiguationData":[TD([[makeQuery(id+"F0.imprint","IMPRINT",EDGE,{"disambiguationData":[TD([[subQ2,-1.0]])],"derivedFrom":subQ1}),-1.0]])]});}
            var Q56;
            {var subQ0=sQuery(id+"F0.wireOp",EDGE,"E6");var subQ1=sQuery(id+"F0.wireOp",EDGE,"E1");var subQ2=makeQuery(id+"F0.imprint","INTERSECT",VERTEX,{"derivedFrom":[subQ1,subQ0]});Q56=makeQuery(id+"F0.imprint","IMPRINT",FACE,{"disambiguationData":[TD([[makeQuery(id+"F0.imprint","IMPRINT",EDGE,{"disambiguationData":[TD([[subQ2,-1.0]])],"derivedFrom":subQ1}),1.0]])]});}
            var Q57;
            {var subQ0=sQuery(id+"F0.wireOp",EDGE,"E22");var subQ1=sQuery(id+"F0.wireOp",EDGE,"E1");var subQ2=makeQuery(id+"F0.imprint","INTERSECT",VERTEX,{"disambiguationData":[OD(0.0)],"derivedFrom":[subQ1,subQ0]});Q57=makeQuery(id+"F0.imprint","IMPRINT",FACE,{"disambiguationData":[TD([[makeQuery(id+"F0.imprint","IMPRINT",EDGE,{"disambiguationData":[TD([[subQ2,-1.0]])],"derivedFrom":subQ1}),-1.0]])]});}
            var Q58;
            {var subQ0=sQuery(id+"F0.wireOp",EDGE,"E22");var subQ1=sQuery(id+"F0.wireOp",EDGE,"E1");var subQ2=makeQuery(id+"F0.imprint","INTERSECT",VERTEX,{"disambiguationData":[OD(0.0)],"derivedFrom":[subQ1,subQ0]});Q58=makeQuery(id+"F0.imprint","IMPRINT",FACE,{"disambiguationData":[TD([[makeQuery(id+"F0.imprint","IMPRINT",EDGE,{"disambiguationData":[TD([[subQ2,-1.0]])],"derivedFrom":subQ1}),1.0]])]});}
            var Q59;
            {var subQ0=sQuery(id+"F0.wireOp",EDGE,"E15");var subQ1=sQuery(id+"F0.wireOp",EDGE,"E1");var subQ2=makeQuery(id+"F0.imprint","INTERSECT",VERTEX,{"disambiguationData":[OD(0.0)],"derivedFrom":[subQ1,subQ0]});Q59=makeQuery(id+"F0.imprint","IMPRINT",FACE,{"disambiguationData":[TD([[makeQuery(id+"F0.imprint","IMPRINT",EDGE,{"disambiguationData":[TD([[subQ2,-1.0]])],"derivedFrom":subQ1}),-1.0]])]});}
            var Q60;
            {var subQ0=sQuery(id+"F0.wireOp",EDGE,"E12");var subQ1=sQuery(id+"F0.wireOp",EDGE,"E1");var subQ2=makeQuery(id+"F0.imprint","INTERSECT",VERTEX,{"disambiguationData":[OD(0.0)],"derivedFrom":[subQ1,subQ0]});Q60=makeQuery(id+"F0.imprint","IMPRINT",FACE,{"disambiguationData":[TD([[makeQuery(id+"F0.imprint","IMPRINT",EDGE,{"disambiguationData":[TD([[subQ2,-1.0]])],"derivedFrom":subQ1}),1.0]])]});}
            var Q61;
            {var subQ0=sQuery(id+"F0.wireOp",EDGE,"E30");var subQ1=sQuery(id+"F0.wireOp",EDGE,"E1");var subQ2=makeQuery(id+"F0.imprint","INTERSECT",VERTEX,{"disambiguationData":[OD(0.0)],"derivedFrom":[subQ1,subQ0]});Q61=makeQuery(id+"F0.imprint","IMPRINT",FACE,{"disambiguationData":[TD([[makeQuery(id+"F0.imprint","IMPRINT",EDGE,{"disambiguationData":[TD([[subQ2,-1.0]])],"derivedFrom":subQ1}),1.0]])]});}
            var Q62;
            {var subQ0=sQuery(id+"F0.wireOp",EDGE,"E30");var subQ1=sQuery(id+"F0.wireOp",EDGE,"E1");var subQ2=makeQuery(id+"F0.imprint","INTERSECT",VERTEX,{"disambiguationData":[OD(0.0)],"derivedFrom":[subQ1,subQ0]});Q62=makeQuery(id+"F0.imprint","IMPRINT",FACE,{"disambiguationData":[TD([[makeQuery(id+"F0.imprint","IMPRINT",EDGE,{"disambiguationData":[TD([[subQ2,-1.0]])],"derivedFrom":subQ1}),-1.0]])]});}
            var Q63;
            {var subQ0=sQuery(id+"F0.wireOp",EDGE,"E12");var subQ1=sQuery(id+"F0.wireOp",EDGE,"E1");var subQ2=makeQuery(id+"F0.imprint","INTERSECT",VERTEX,{"disambiguationData":[OD(1.0)],"derivedFrom":[subQ1,subQ0]});Q63=makeQuery(id+"F0.imprint","IMPRINT",FACE,{"disambiguationData":[TD([[makeQuery(id+"F0.imprint","IMPRINT",EDGE,{"disambiguationData":[TD([[subQ2,-1.0]])],"derivedFrom":subQ1}),1.0]])]});}
            var Q64;
            {var subQ9=sQuery(id+"F0.wireOp",EDGE,"E1");var subQ12=sQuery(id+"F0.wireOp",EDGE,"E15");var subQ14=makeQuery(id+"F0.imprint","INTERSECT",VERTEX,{"disambiguationData":[OD(1.0)],"derivedFrom":[subQ9,subQ12]});Q64=makeQuery(id+"F0.imprint","IMPRINT",FACE,{"disambiguationData":[TD([[makeQuery(id+"F0.imprint","IMPRINT",EDGE,{"disambiguationData":[TD([[subQ14,-1.0]])],"derivedFrom":subQ9}),-1.0]])]});}
            var Q65;
            {var subQ0=sQuery(id+"F0.wireOp",EDGE,"E12");var subQ1=sQuery(id+"F0.wireOp",EDGE,"E1");var subQ2=makeQuery(id+"F0.imprint","INTERSECT",VERTEX,{"disambiguationData":[OD(0.0)],"derivedFrom":[subQ1,subQ0]});Q65=makeQuery(id+"F0.imprint","IMPRINT",FACE,{"disambiguationData":[TD([[makeQuery(id+"F0.imprint","IMPRINT",EDGE,{"disambiguationData":[TD([[subQ2,-1.0]])],"derivedFrom":subQ1}),-1.0]])]});}
            var Q66;
            {var subQ0=sQuery(id+"F0.wireOp",EDGE,"E29");var subQ1=sQuery(id+"F0.wireOp",EDGE,"E2");var subQ2=makeQuery(id+"F0.imprint","INTERSECT",VERTEX,{"disambiguationData":[OD(0.0)],"derivedFrom":[subQ1,subQ0]});Q66=makeQuery(id+"F0.imprint","IMPRINT",FACE,{"disambiguationData":[TD([[makeQuery(id+"F0.imprint","IMPRINT",EDGE,{"disambiguationData":[TD([[subQ2,-1.0]])],"derivedFrom":subQ1}),1.0]])]});}
            var Q67;
            {var subQ0=sQuery(id+"F0.wireOp",EDGE,"E29");var subQ1=sQuery(id+"F0.wireOp",EDGE,"E2");var subQ2=makeQuery(id+"F0.imprint","INTERSECT",VERTEX,{"disambiguationData":[OD(0.0)],"derivedFrom":[subQ1,subQ0]});Q67=makeQuery(id+"F0.imprint","IMPRINT",FACE,{"disambiguationData":[TD([[makeQuery(id+"F0.imprint","IMPRINT",EDGE,{"disambiguationData":[TD([[subQ2,-1.0]])],"derivedFrom":subQ1}),-1.0]])]});}
            var Q68;
            {var subQ0=sQuery(id+"F0.wireOp",EDGE,"E12");var subQ1=sQuery(id+"F0.wireOp",EDGE,"E2");var subQ2=makeQuery(id+"F0.imprint","INTERSECT",VERTEX,{"disambiguationData":[OD(1.0)],"derivedFrom":[subQ1,subQ0]});Q68=makeQuery(id+"F0.imprint","IMPRINT",FACE,{"disambiguationData":[TD([[makeQuery(id+"F0.imprint","IMPRINT",EDGE,{"disambiguationData":[TD([[subQ2,-1.0]])],"derivedFrom":subQ1}),-1.0]])]});}
            var Q69;
            {var subQ0=sQuery(id+"F0.wireOp",EDGE,"E28");var subQ1=sQuery(id+"F0.wireOp",EDGE,"E3");var subQ2=makeQuery(id+"F0.imprint","INTERSECT",VERTEX,{"disambiguationData":[OD(0.0)],"derivedFrom":[subQ1,subQ0]});Q69=makeQuery(id+"F0.imprint","IMPRINT",FACE,{"disambiguationData":[TD([[makeQuery(id+"F0.imprint","IMPRINT",EDGE,{"disambiguationData":[TD([[subQ2,-1.0]])],"derivedFrom":subQ1}),1.0]])]});}
            var Q70;
            {var subQ0=sQuery(id+"F0.wireOp",EDGE,"E12");var subQ1=sQuery(id+"F0.wireOp",EDGE,"E3");var subQ2=makeQuery(id+"F0.imprint","INTERSECT",VERTEX,{"disambiguationData":[OD(1.0)],"derivedFrom":[subQ1,subQ0]});Q70=makeQuery(id+"F0.imprint","IMPRINT",FACE,{"disambiguationData":[TD([[makeQuery(id+"F0.imprint","IMPRINT",EDGE,{"disambiguationData":[TD([[subQ2,-1.0]])],"derivedFrom":subQ1}),1.0]])]});}
            var Q71;
            {var subQ0=sQuery(id+"F0.wireOp",EDGE,"E28");var subQ1=sQuery(id+"F0.wireOp",EDGE,"E3");var subQ2=makeQuery(id+"F0.imprint","INTERSECT",VERTEX,{"disambiguationData":[OD(0.0)],"derivedFrom":[subQ1,subQ0]});Q71=makeQuery(id+"F0.imprint","IMPRINT",FACE,{"disambiguationData":[TD([[makeQuery(id+"F0.imprint","IMPRINT",EDGE,{"disambiguationData":[TD([[subQ2,-1.0]])],"derivedFrom":subQ1}),-1.0]])]});}
            var Q72;
            {var subQ0=sQuery(id+"F0.wireOp",EDGE,"E27");var subQ1=sQuery(id+"F0.wireOp",EDGE,"E4");var subQ2=makeQuery(id+"F0.imprint","INTERSECT",VERTEX,{"disambiguationData":[OD(0.0)],"derivedFrom":[subQ1,subQ0]});Q72=makeQuery(id+"F0.imprint","IMPRINT",FACE,{"disambiguationData":[TD([[makeQuery(id+"F0.imprint","IMPRINT",EDGE,{"disambiguationData":[TD([[subQ2,-1.0]])],"derivedFrom":subQ1}),1.0]])]});}
            var Q73;
            {var subQ0=sQuery(id+"F0.wireOp",EDGE,"E27");var subQ1=sQuery(id+"F0.wireOp",EDGE,"E4");var subQ2=makeQuery(id+"F0.imprint","INTERSECT",VERTEX,{"disambiguationData":[OD(0.0)],"derivedFrom":[subQ1,subQ0]});Q73=makeQuery(id+"F0.imprint","IMPRINT",FACE,{"disambiguationData":[TD([[makeQuery(id+"F0.imprint","IMPRINT",EDGE,{"disambiguationData":[TD([[subQ2,-1.0]])],"derivedFrom":subQ1}),-1.0]])]});}
            var Q74;
            {var subQ0=sQuery(id+"F0.wireOp",EDGE,"E12");var subQ1=sQuery(id+"F0.wireOp",EDGE,"E4");var subQ2=makeQuery(id+"F0.imprint","INTERSECT",VERTEX,{"disambiguationData":[OD(1.0)],"derivedFrom":[subQ1,subQ0]});Q74=makeQuery(id+"F0.imprint","IMPRINT",FACE,{"disambiguationData":[TD([[makeQuery(id+"F0.imprint","IMPRINT",EDGE,{"disambiguationData":[TD([[subQ2,-1.0]])],"derivedFrom":subQ1}),-1.0]])]});}
            var Q75;
            {var subQ0=sQuery(id+"F0.wireOp",EDGE,"E6");var subQ1=sQuery(id+"F0.wireOp",EDGE,"E4");var subQ2=makeQuery(id+"F0.imprint","INTERSECT",VERTEX,{"derivedFrom":[subQ1,subQ0]});Q75=makeQuery(id+"F0.imprint","IMPRINT",FACE,{"disambiguationData":[TD([[makeQuery(id+"F0.imprint","IMPRINT",EDGE,{"disambiguationData":[TD([[subQ2,-1.0]])],"derivedFrom":subQ1}),-1.0]])]});}
            var Q76;
            {var subQ0=sQuery(id+"F0.wireOp",EDGE,"E6");var subQ1=sQuery(id+"F0.wireOp",EDGE,"E4");var subQ2=makeQuery(id+"F0.imprint","INTERSECT",VERTEX,{"derivedFrom":[subQ1,subQ0]});Q76=makeQuery(id+"F0.imprint","IMPRINT",FACE,{"disambiguationData":[TD([[makeQuery(id+"F0.imprint","IMPRINT",EDGE,{"disambiguationData":[TD([[subQ2,-1.0]])],"derivedFrom":subQ1}),1.0]])]});}
            var Q77;
            {var subQ0=sQuery(id+"F0.wireOp",EDGE,"E26");var subQ1=sQuery(id+"F0.wireOp",EDGE,"E4");var subQ2=makeQuery(id+"F0.imprint","INTERSECT",VERTEX,{"disambiguationData":[OD(0.0)],"derivedFrom":[subQ1,subQ0]});Q77=makeQuery(id+"F0.imprint","IMPRINT",FACE,{"disambiguationData":[TD([[makeQuery(id+"F0.imprint","IMPRINT",EDGE,{"disambiguationData":[TD([[subQ2,-1.0]])],"derivedFrom":subQ1}),1.0]])]});}
            var Q78;
            {var subQ0=sQuery(id+"F0.wireOp",EDGE,"E25");var subQ1=sQuery(id+"F0.wireOp",EDGE,"E3");var subQ2=makeQuery(id+"F0.imprint","INTERSECT",VERTEX,{"disambiguationData":[OD(0.0)],"derivedFrom":[subQ1,subQ0]});Q78=makeQuery(id+"F0.imprint","IMPRINT",FACE,{"disambiguationData":[TD([[makeQuery(id+"F0.imprint","IMPRINT",EDGE,{"disambiguationData":[TD([[subQ2,-1.0]])],"derivedFrom":subQ1}),-1.0]])]});}
            var Q79;
            {var subQ0=sQuery(id+"F0.wireOp",EDGE,"E6");var subQ1=sQuery(id+"F0.wireOp",EDGE,"E3");var subQ2=makeQuery(id+"F0.imprint","INTERSECT",VERTEX,{"derivedFrom":[subQ1,subQ0]});Q79=makeQuery(id+"F0.imprint","IMPRINT",FACE,{"disambiguationData":[TD([[makeQuery(id+"F0.imprint","IMPRINT",EDGE,{"disambiguationData":[TD([[subQ2,-1.0]])],"derivedFrom":subQ1}),-1.0]])]});}
            var Q80;
            {var subQ0=sQuery(id+"F0.wireOp",EDGE,"E6");var subQ1=sQuery(id+"F0.wireOp",EDGE,"E3");var subQ2=makeQuery(id+"F0.imprint","INTERSECT",VERTEX,{"derivedFrom":[subQ1,subQ0]});Q80=makeQuery(id+"F0.imprint","IMPRINT",FACE,{"disambiguationData":[TD([[makeQuery(id+"F0.imprint","IMPRINT",EDGE,{"disambiguationData":[TD([[subQ2,-1.0]])],"derivedFrom":subQ1}),1.0]])]});}
            var Q81;
            {var subQ0=sQuery(id+"F0.wireOp",EDGE,"E24");var subQ1=sQuery(id+"F0.wireOp",EDGE,"E2");var subQ2=makeQuery(id+"F0.imprint","INTERSECT",VERTEX,{"disambiguationData":[OD(0.0)],"derivedFrom":[subQ1,subQ0]});Q81=makeQuery(id+"F0.imprint","IMPRINT",FACE,{"disambiguationData":[TD([[makeQuery(id+"F0.imprint","IMPRINT",EDGE,{"disambiguationData":[TD([[subQ2,-1.0]])],"derivedFrom":subQ1}),1.0]])]});}
            var Q82;
            {var subQ0=sQuery(id+"F0.wireOp",EDGE,"E6");var subQ1=sQuery(id+"F0.wireOp",EDGE,"E2");var subQ2=makeQuery(id+"F0.imprint","INTERSECT",VERTEX,{"derivedFrom":[subQ1,subQ0]});Q82=makeQuery(id+"F0.imprint","IMPRINT",FACE,{"disambiguationData":[TD([[makeQuery(id+"F0.imprint","IMPRINT",EDGE,{"disambiguationData":[TD([[subQ2,-1.0]])],"derivedFrom":subQ1}),1.0]])]});}
            var Q83;
            {var subQ0=sQuery(id+"F0.wireOp",EDGE,"E6");var subQ1=sQuery(id+"F0.wireOp",EDGE,"E2");var subQ2=makeQuery(id+"F0.imprint","INTERSECT",VERTEX,{"derivedFrom":[subQ1,subQ0]});Q83=makeQuery(id+"F0.imprint","IMPRINT",FACE,{"disambiguationData":[TD([[makeQuery(id+"F0.imprint","IMPRINT",EDGE,{"disambiguationData":[TD([[subQ2,-1.0]])],"derivedFrom":subQ1}),-1.0]])]});}
            var Q84;
            {var subQ0=sQuery(id+"F0.wireOp",EDGE,"E6");var subQ1=sQuery(id+"F0.wireOp",EDGE,"E1");var subQ2=makeQuery(id+"F0.imprint","INTERSECT",VERTEX,{"derivedFrom":[subQ1,subQ0]});Q84=makeQuery(id+"F0.imprint","IMPRINT",FACE,{"disambiguationData":[TD([[makeQuery(id+"F0.imprint","IMPRINT",EDGE,{"disambiguationData":[TD([[subQ2,-1.0]])],"derivedFrom":subQ1}),-1.0]])]});}
            var Q85;
            {var subQ0=sQuery(id+"F0.wireOp",EDGE,"E10");var subQ1=sQuery(id+"F0.wireOp",EDGE,"E1");var subQ2=makeQuery(id+"F0.imprint","INTERSECT",VERTEX,{"derivedFrom":[subQ1,subQ0]});Q85=makeQuery(id+"F0.imprint","IMPRINT",FACE,{"disambiguationData":[TD([[makeQuery(id+"F0.imprint","IMPRINT",EDGE,{"disambiguationData":[TD([[subQ2,-1.0]])],"derivedFrom":subQ1}),1.0]])]});}
            var Q86;
            {var subQ0=sQuery(id+"F0.wireOp",EDGE,"E21");var subQ1=sQuery(id+"F0.wireOp",EDGE,"E2");var subQ2=makeQuery(id+"F0.imprint","INTERSECT",VERTEX,{"disambiguationData":[OD(0.0)],"derivedFrom":[subQ1,subQ0]});Q86=makeQuery(id+"F0.imprint","IMPRINT",FACE,{"disambiguationData":[TD([[makeQuery(id+"F0.imprint","IMPRINT",EDGE,{"disambiguationData":[TD([[subQ2,-1.0]])],"derivedFrom":subQ1}),-1.0]])]});}
            var Q87;
            {var subQ0=sQuery(id+"F0.wireOp",EDGE,"E21");var subQ1=sQuery(id+"F0.wireOp",EDGE,"E2");var subQ2=makeQuery(id+"F0.imprint","INTERSECT",VERTEX,{"disambiguationData":[OD(0.0)],"derivedFrom":[subQ1,subQ0]});Q87=makeQuery(id+"F0.imprint","IMPRINT",FACE,{"disambiguationData":[TD([[makeQuery(id+"F0.imprint","IMPRINT",EDGE,{"disambiguationData":[TD([[subQ2,-1.0]])],"derivedFrom":subQ1}),1.0]])]});}
            var Q88;
            {var subQ0=sQuery(id+"F0.wireOp",EDGE,"E10");var subQ1=sQuery(id+"F0.wireOp",EDGE,"E2");var subQ2=makeQuery(id+"F0.imprint","INTERSECT",VERTEX,{"derivedFrom":[subQ1,subQ0]});Q88=makeQuery(id+"F0.imprint","IMPRINT",FACE,{"disambiguationData":[TD([[makeQuery(id+"F0.imprint","IMPRINT",EDGE,{"disambiguationData":[TD([[subQ2,-1.0]])],"derivedFrom":subQ1}),-1.0]])]});}
            var Q89;
            {var subQ0=sQuery(id+"F0.wireOp",EDGE,"E20");var subQ1=sQuery(id+"F0.wireOp",EDGE,"E3");var subQ2=makeQuery(id+"F0.imprint","INTERSECT",VERTEX,{"disambiguationData":[OD(0.0)],"derivedFrom":[subQ1,subQ0]});Q89=makeQuery(id+"F0.imprint","IMPRINT",FACE,{"disambiguationData":[TD([[makeQuery(id+"F0.imprint","IMPRINT",EDGE,{"disambiguationData":[TD([[subQ2,-1.0]])],"derivedFrom":subQ1}),-1.0]])]});}
            var Q90;
            {var subQ0=sQuery(id+"F0.wireOp",EDGE,"E20");var subQ1=sQuery(id+"F0.wireOp",EDGE,"E3");var subQ2=makeQuery(id+"F0.imprint","INTERSECT",VERTEX,{"disambiguationData":[OD(0.0)],"derivedFrom":[subQ1,subQ0]});Q90=makeQuery(id+"F0.imprint","IMPRINT",FACE,{"disambiguationData":[TD([[makeQuery(id+"F0.imprint","IMPRINT",EDGE,{"disambiguationData":[TD([[subQ2,-1.0]])],"derivedFrom":subQ1}),1.0]])]});}
            var Q91;
            {var subQ0=sQuery(id+"F0.wireOp",EDGE,"E10");var subQ1=sQuery(id+"F0.wireOp",EDGE,"E3");var subQ2=makeQuery(id+"F0.imprint","INTERSECT",VERTEX,{"derivedFrom":[subQ1,subQ0]});Q91=makeQuery(id+"F0.imprint","IMPRINT",FACE,{"disambiguationData":[TD([[makeQuery(id+"F0.imprint","IMPRINT",EDGE,{"disambiguationData":[TD([[subQ2,-1.0]])],"derivedFrom":subQ1}),1.0]])]});}
            var Q92;
            {var subQ0=sQuery(id+"F0.wireOp",EDGE,"E10");var subQ1=sQuery(id+"F0.wireOp",EDGE,"E4");var subQ2=makeQuery(id+"F0.imprint","INTERSECT",VERTEX,{"derivedFrom":[subQ1,subQ0]});Q92=makeQuery(id+"F0.imprint","IMPRINT",FACE,{"disambiguationData":[TD([[makeQuery(id+"F0.imprint","IMPRINT",EDGE,{"disambiguationData":[TD([[subQ2,-1.0]])],"derivedFrom":subQ1}),-1.0]])]});}
            var Q93;
            {var subQ0=sQuery(id+"F0.wireOp",EDGE,"E19");var subQ1=sQuery(id+"F0.wireOp",EDGE,"E4");var subQ2=makeQuery(id+"F0.imprint","INTERSECT",VERTEX,{"disambiguationData":[OD(0.0)],"derivedFrom":[subQ1,subQ0]});Q93=makeQuery(id+"F0.imprint","IMPRINT",FACE,{"disambiguationData":[TD([[makeQuery(id+"F0.imprint","IMPRINT",EDGE,{"disambiguationData":[TD([[subQ2,-1.0]])],"derivedFrom":subQ1}),1.0]])]});}
            var Q94;
            {var subQ0=sQuery(id+"F0.wireOp",EDGE,"E12");var subQ1=sQuery(id+"F0.wireOp",EDGE,"E2");var subQ2=makeQuery(id+"F0.imprint","INTERSECT",VERTEX,{"disambiguationData":[OD(0.0)],"derivedFrom":[subQ1,subQ0]});Q94=makeQuery(id+"F0.imprint","IMPRINT",FACE,{"disambiguationData":[TD([[makeQuery(id+"F0.imprint","IMPRINT",EDGE,{"disambiguationData":[TD([[subQ2,-1.0]])],"derivedFrom":subQ1}),-1.0]])]});}
            var Q95;
            {var subQ0=sQuery(id+"F0.wireOp",EDGE,"E12");var subQ1=sQuery(id+"F0.wireOp",EDGE,"E2");var subQ2=makeQuery(id+"F0.imprint","INTERSECT",VERTEX,{"disambiguationData":[OD(0.0)],"derivedFrom":[subQ1,subQ0]});Q95=makeQuery(id+"F0.imprint","IMPRINT",FACE,{"disambiguationData":[TD([[makeQuery(id+"F0.imprint","IMPRINT",EDGE,{"disambiguationData":[TD([[subQ2,-1.0]])],"derivedFrom":subQ1}),1.0]])]});}
            var Q96;
            {var subQ0=sQuery(id+"F0.wireOp",EDGE,"E16");var subQ1=sQuery(id+"F0.wireOp",EDGE,"E2");var subQ2=makeQuery(id+"F0.imprint","INTERSECT",VERTEX,{"disambiguationData":[OD(0.0)],"derivedFrom":[subQ1,subQ0]});Q96=makeQuery(id+"F0.imprint","IMPRINT",FACE,{"disambiguationData":[TD([[makeQuery(id+"F0.imprint","IMPRINT",EDGE,{"disambiguationData":[TD([[subQ2,-1.0]])],"derivedFrom":subQ1}),1.0]])]});}
            var Q97;
            {var subQ0=sQuery(id+"F0.wireOp",EDGE,"E17");var subQ1=sQuery(id+"F0.wireOp",EDGE,"E3");var subQ2=makeQuery(id+"F0.imprint","INTERSECT",VERTEX,{"disambiguationData":[OD(0.0)],"derivedFrom":[subQ1,subQ0]});Q97=makeQuery(id+"F0.imprint","IMPRINT",FACE,{"disambiguationData":[TD([[makeQuery(id+"F0.imprint","IMPRINT",EDGE,{"disambiguationData":[TD([[subQ2,-1.0]])],"derivedFrom":subQ1}),-1.0]])]});}
            var Q98;
            {var subQ0=sQuery(id+"F0.wireOp",EDGE,"E12");var subQ1=sQuery(id+"F0.wireOp",EDGE,"E3");var subQ2=makeQuery(id+"F0.imprint","INTERSECT",VERTEX,{"disambiguationData":[OD(0.0)],"derivedFrom":[subQ1,subQ0]});Q98=makeQuery(id+"F0.imprint","IMPRINT",FACE,{"disambiguationData":[TD([[makeQuery(id+"F0.imprint","IMPRINT",EDGE,{"disambiguationData":[TD([[subQ2,-1.0]])],"derivedFrom":subQ1}),-1.0]])]});}
            var Q99;
            {var subQ0=sQuery(id+"F0.wireOp",EDGE,"E12");var subQ1=sQuery(id+"F0.wireOp",EDGE,"E3");var subQ2=makeQuery(id+"F0.imprint","INTERSECT",VERTEX,{"disambiguationData":[OD(0.0)],"derivedFrom":[subQ1,subQ0]});Q99=makeQuery(id+"F0.imprint","IMPRINT",FACE,{"disambiguationData":[TD([[makeQuery(id+"F0.imprint","IMPRINT",EDGE,{"disambiguationData":[TD([[subQ2,-1.0]])],"derivedFrom":subQ1}),1.0]])]});}
            var Q100;
            {var subQ0=sQuery(id+"F0.wireOp",EDGE,"E12");var subQ1=sQuery(id+"F0.wireOp",EDGE,"E4");var subQ2=makeQuery(id+"F0.imprint","INTERSECT",VERTEX,{"disambiguationData":[OD(0.0)],"derivedFrom":[subQ1,subQ0]});Q100=makeQuery(id+"F0.imprint","IMPRINT",FACE,{"disambiguationData":[TD([[makeQuery(id+"F0.imprint","IMPRINT",EDGE,{"disambiguationData":[TD([[subQ2,-1.0]])],"derivedFrom":subQ1}),-1.0]])]});}
            var Q101;
            {var subQ0=sQuery(id+"F0.wireOp",EDGE,"E12");var subQ1=sQuery(id+"F0.wireOp",EDGE,"E4");var subQ2=makeQuery(id+"F0.imprint","INTERSECT",VERTEX,{"disambiguationData":[OD(0.0)],"derivedFrom":[subQ1,subQ0]});Q101=makeQuery(id+"F0.imprint","IMPRINT",FACE,{"disambiguationData":[TD([[makeQuery(id+"F0.imprint","IMPRINT",EDGE,{"disambiguationData":[TD([[subQ2,-1.0]])],"derivedFrom":subQ1}),1.0]])]});}
            var Q102;
            {var subQ0=sQuery(id+"F0.wireOp",EDGE,"E18");var subQ1=sQuery(id+"F0.wireOp",EDGE,"E4");var subQ2=makeQuery(id+"F0.imprint","INTERSECT",VERTEX,{"disambiguationData":[OD(0.0)],"derivedFrom":[subQ1,subQ0]});Q102=makeQuery(id+"F0.imprint","IMPRINT",FACE,{"disambiguationData":[TD([[makeQuery(id+"F0.imprint","IMPRINT",EDGE,{"disambiguationData":[TD([[subQ2,-1.0]])],"derivedFrom":subQ1}),1.0]])]});}
            var Q103;
            {var subQ0=sQuery(id+"F0.wireOp",EDGE,"E19");var subQ1=sQuery(id+"F0.wireOp",EDGE,"E4");var subQ2=makeQuery(id+"F0.imprint","INTERSECT",VERTEX,{"disambiguationData":[OD(0.0)],"derivedFrom":[subQ1,subQ0]});Q103=makeQuery(id+"F0.imprint","IMPRINT",FACE,{"disambiguationData":[TD([[makeQuery(id+"F0.imprint","IMPRINT",EDGE,{"disambiguationData":[TD([[subQ2,-1.0]])],"derivedFrom":subQ1}),-1.0]])]});}
            var Q104;
            {var subQ0=sQuery(id+"F0.wireOp",EDGE,"E49");Q104=makeQuery(id+"F0.imprint","IMPRINT",FACE,{"disambiguationData":[TD([[makeQuery(id+"F0.imprint","IMPRINT",EDGE,{"derivedFrom":subQ0}),1.0]])]});}
            var Q105;
            {var subQ0=sQuery(id+"F0.wireOp",EDGE,"E48");Q105=makeQuery(id+"F0.imprint","IMPRINT",FACE,{"disambiguationData":[TD([[makeQuery(id+"F0.imprint","IMPRINT",EDGE,{"derivedFrom":subQ0}),-1.0]])]});}
            var Q106;
            {var subQ0=sQuery(id+"F0.wireOp",EDGE,"E47");Q106=makeQuery(id+"F0.imprint","IMPRINT",FACE,{"disambiguationData":[TD([[makeQuery(id+"F0.imprint","IMPRINT",EDGE,{"derivedFrom":subQ0}),-1.0]])]});}
            var Q107;
            {var subQ0=sQuery(id+"F0.wireOp",EDGE,"E46");Q107=makeQuery(id+"F0.imprint","IMPRINT",FACE,{"disambiguationData":[TD([[makeQuery(id+"F0.imprint","IMPRINT",EDGE,{"derivedFrom":subQ0}),1.0]])]});}
            extrude(context, id + "F1", {"entities" : qUnion([Q0, Q1, Q2, Q3, Q4, Q5, Q6, Q7, Q8, Q9, Q10, Q11, Q12, Q13, Q14, Q15, Q16, Q17, Q18, Q19, Q20, Q21, Q22, Q23, Q24, Q25, Q26, Q27, Q28, Q29, Q30, Q31, Q32, Q33, Q34, Q35, Q36, Q37, Q38, Q39, Q40, Q41, Q42, Q43, Q44, Q45, Q46, Q47, Q48, Q49, Q50, Q51, Q52, Q53, Q54, Q55, Q56, Q57, Q58, Q59, Q60, Q61, Q62, Q63, Q64, Q65, Q66, Q67, Q68, Q69, Q70, Q71, Q72, Q73, Q74, Q75, Q76, Q77, Q78, Q79, Q80, Q81, Q82, Q83, Q84, Q85, Q86, Q87, Q88, Q89, Q90, Q91, Q92, Q93, Q94, Q95, Q96, Q97, Q98, Q99, Q100, Q101, Q102, Q103, Q104, Q105, Q106, Q107]), "depth" : 1.52 * mm, "offsetDistance" : 25.4 * mm});
        }
        {
            var Q0;
            {var subQ0=sQuery(id+"F0.wireOp",EDGE,"E34");var subQ1=sQuery(id+"F0.wireOp",EDGE,"E1");Q0=makeQuery(id+"F1.opExtrude","SWEPT_EDGE",EDGE,{"disambiguationData":[OSD([subQ1,subQ0]),TDD([makeQuery(id+"F0.imprint","INTERSECT",VERTEX,{"disambiguationData":[OD(1.0)],"derivedFrom":[subQ1,subQ0]})])]});}
            var Q1;
            {var subQ0=sQuery(id+"F0.wireOp",EDGE,"E34");var subQ1=sQuery(id+"F0.wireOp",EDGE,"E8");Q1=makeQuery(id+"F1.opExtrude","SWEPT_EDGE",EDGE,{"disambiguationData":[OSD([subQ1,subQ0]),TDD([makeQuery(id+"F0.imprint","INTERSECT",VERTEX,{"disambiguationData":[OD(0.0)],"derivedFrom":[subQ1,subQ0]})])]});}
            var Q2;
            {var subQ0=sQuery(id+"F0.wireOp",EDGE,"E32");var subQ1=sQuery(id+"F0.wireOp",EDGE,"E3");Q2=makeQuery(id+"F1.opExtrude","SWEPT_EDGE",EDGE,{"disambiguationData":[OSD([subQ1,subQ0]),TDD([makeQuery(id+"F0.imprint","INTERSECT",VERTEX,{"disambiguationData":[OD(1.0)],"derivedFrom":[subQ1,subQ0]})])]});}
            var Q3;
            {var subQ0=sQuery(id+"F0.wireOp",EDGE,"E32");var subQ1=sQuery(id+"F0.wireOp",EDGE,"E8");Q3=makeQuery(id+"F1.opExtrude","SWEPT_EDGE",EDGE,{"disambiguationData":[OSD([subQ1,subQ0]),TDD([makeQuery(id+"F0.imprint","INTERSECT",VERTEX,{"disambiguationData":[OD(0.0)],"derivedFrom":[subQ1,subQ0]})])]});}
            var Q4;
            {var subQ0=sQuery(id+"F0.wireOp",EDGE,"E37");var subQ1=sQuery(id+"F0.wireOp",EDGE,"E3");Q4=makeQuery(id+"F1.opExtrude","SWEPT_EDGE",EDGE,{"disambiguationData":[OSD([subQ1,subQ0]),TDD([makeQuery(id+"F0.imprint","INTERSECT",VERTEX,{"disambiguationData":[OD(1.0)],"derivedFrom":[subQ1,subQ0]})])]});}
            var Q5;
            {var subQ0=sQuery(id+"F0.wireOp",EDGE,"E37");var subQ1=sQuery(id+"F0.wireOp",EDGE,"E8");Q5=makeQuery(id+"F1.opExtrude","SWEPT_EDGE",EDGE,{"disambiguationData":[OSD([subQ1,subQ0]),TDD([makeQuery(id+"F0.imprint","INTERSECT",VERTEX,{"disambiguationData":[OD(0.0)],"derivedFrom":[subQ1,subQ0]})])]});}
            var Q6;
            {var subQ0=sQuery(id+"F0.wireOp",EDGE,"E35");var subQ1=sQuery(id+"F0.wireOp",EDGE,"E1");Q6=makeQuery(id+"F1.opExtrude","SWEPT_EDGE",EDGE,{"disambiguationData":[OSD([subQ1,subQ0]),TDD([makeQuery(id+"F0.imprint","INTERSECT",VERTEX,{"disambiguationData":[OD(1.0)],"derivedFrom":[subQ1,subQ0]})])]});}
            var Q7;
            {var subQ0=sQuery(id+"F0.wireOp",EDGE,"E35");var subQ1=sQuery(id+"F0.wireOp",EDGE,"E8");Q7=makeQuery(id+"F1.opExtrude","SWEPT_EDGE",EDGE,{"disambiguationData":[OSD([subQ1,subQ0]),TDD([makeQuery(id+"F0.imprint","INTERSECT",VERTEX,{"disambiguationData":[OD(0.0)],"derivedFrom":[subQ1,subQ0]})])]});}
            var Q8;
            {var subQ0=sQuery(id+"F0.wireOp",EDGE,"E38");var subQ1=sQuery(id+"F0.wireOp",EDGE,"E8");Q8=makeQuery(id+"F1.opExtrude","SWEPT_EDGE",EDGE,{"disambiguationData":[OSD([subQ1,subQ0]),TDD([makeQuery(id+"F0.imprint","INTERSECT",VERTEX,{"disambiguationData":[OD(1.0)],"derivedFrom":[subQ1,subQ0]})])]});}
            var Q9;
            {var subQ0=sQuery(id+"F0.wireOp",EDGE,"E38");var subQ1=sQuery(id+"F0.wireOp",EDGE,"E4");Q9=makeQuery(id+"F1.opExtrude","SWEPT_EDGE",EDGE,{"disambiguationData":[OSD([subQ1,subQ0]),TDD([makeQuery(id+"F0.imprint","INTERSECT",VERTEX,{"disambiguationData":[OD(1.0)],"derivedFrom":[subQ1,subQ0]})])]});}
            var Q10;
            {var subQ0=sQuery(id+"F0.wireOp",EDGE,"E36");var subQ1=sQuery(id+"F0.wireOp",EDGE,"E8");Q10=makeQuery(id+"F1.opExtrude","SWEPT_EDGE",EDGE,{"disambiguationData":[OSD([subQ1,subQ0]),TDD([makeQuery(id+"F0.imprint","INTERSECT",VERTEX,{"disambiguationData":[OD(1.0)],"derivedFrom":[subQ1,subQ0]})])]});}
            var Q11;
            {var subQ0=sQuery(id+"F0.wireOp",EDGE,"E36");var subQ1=sQuery(id+"F0.wireOp",EDGE,"E2");Q11=makeQuery(id+"F1.opExtrude","SWEPT_EDGE",EDGE,{"disambiguationData":[OSD([subQ1,subQ0]),TDD([makeQuery(id+"F0.imprint","INTERSECT",VERTEX,{"disambiguationData":[OD(1.0)],"derivedFrom":[subQ1,subQ0]})])]});}
            var Q12;
            {var subQ0=sQuery(id+"F0.wireOp",EDGE,"E33");var subQ1=sQuery(id+"F0.wireOp",EDGE,"E8");Q12=makeQuery(id+"F1.opExtrude","SWEPT_EDGE",EDGE,{"disambiguationData":[OSD([subQ1,subQ0]),TDD([makeQuery(id+"F0.imprint","INTERSECT",VERTEX,{"disambiguationData":[OD(1.0)],"derivedFrom":[subQ1,subQ0]})])]});}
            var Q13;
            {var subQ0=sQuery(id+"F0.wireOp",EDGE,"E33");var subQ1=sQuery(id+"F0.wireOp",EDGE,"E2");Q13=makeQuery(id+"F1.opExtrude","SWEPT_EDGE",EDGE,{"disambiguationData":[OSD([subQ1,subQ0]),TDD([makeQuery(id+"F0.imprint","INTERSECT",VERTEX,{"disambiguationData":[OD(1.0)],"derivedFrom":[subQ1,subQ0]})])]});}
            var Q14;
            {var subQ0=sQuery(id+"F0.wireOp",EDGE,"E31");var subQ1=sQuery(id+"F0.wireOp",EDGE,"E8");Q14=makeQuery(id+"F1.opExtrude","SWEPT_EDGE",EDGE,{"disambiguationData":[OSD([subQ1,subQ0]),TDD([makeQuery(id+"F0.imprint","INTERSECT",VERTEX,{"disambiguationData":[OD(1.0)],"derivedFrom":[subQ1,subQ0]})])]});}
            var Q15;
            {var subQ0=sQuery(id+"F0.wireOp",EDGE,"E31");var subQ1=sQuery(id+"F0.wireOp",EDGE,"E4");Q15=makeQuery(id+"F1.opExtrude","SWEPT_EDGE",EDGE,{"disambiguationData":[OSD([subQ1,subQ0]),TDD([makeQuery(id+"F0.imprint","INTERSECT",VERTEX,{"disambiguationData":[OD(1.0)],"derivedFrom":[subQ1,subQ0]})])]});}
            var Q16;
            {var subQ0=sQuery(id+"F0.wireOp",EDGE,"E31");var subQ1=sQuery(id+"F0.wireOp",EDGE,"E8");Q16=makeQuery(id+"F1.opExtrude","SWEPT_EDGE",EDGE,{"disambiguationData":[OSD([subQ1,subQ0]),TDD([makeQuery(id+"F0.imprint","INTERSECT",VERTEX,{"disambiguationData":[OD(0.0)],"derivedFrom":[subQ1,subQ0]})])]});}
            var Q17;
            {var subQ0=sQuery(id+"F0.wireOp",EDGE,"E31");var subQ1=sQuery(id+"F0.wireOp",EDGE,"E4");Q17=makeQuery(id+"F1.opExtrude","SWEPT_EDGE",EDGE,{"disambiguationData":[OSD([subQ1,subQ0]),TDD([makeQuery(id+"F0.imprint","INTERSECT",VERTEX,{"disambiguationData":[OD(0.0)],"derivedFrom":[subQ1,subQ0]})])]});}
            var Q18;
            {var subQ0=sQuery(id+"F0.wireOp",EDGE,"E33");var subQ1=sQuery(id+"F0.wireOp",EDGE,"E8");Q18=makeQuery(id+"F1.opExtrude","SWEPT_EDGE",EDGE,{"disambiguationData":[OSD([subQ1,subQ0]),TDD([makeQuery(id+"F0.imprint","INTERSECT",VERTEX,{"disambiguationData":[OD(0.0)],"derivedFrom":[subQ1,subQ0]})])]});}
            var Q19;
            {var subQ0=sQuery(id+"F0.wireOp",EDGE,"E33");var subQ1=sQuery(id+"F0.wireOp",EDGE,"E2");Q19=makeQuery(id+"F1.opExtrude","SWEPT_EDGE",EDGE,{"disambiguationData":[OSD([subQ1,subQ0]),TDD([makeQuery(id+"F0.imprint","INTERSECT",VERTEX,{"disambiguationData":[OD(0.0)],"derivedFrom":[subQ1,subQ0]})])]});}
            var Q20;
            {var subQ0=sQuery(id+"F0.wireOp",EDGE,"E36");var subQ1=sQuery(id+"F0.wireOp",EDGE,"E8");Q20=makeQuery(id+"F1.opExtrude","SWEPT_EDGE",EDGE,{"disambiguationData":[OSD([subQ1,subQ0]),TDD([makeQuery(id+"F0.imprint","INTERSECT",VERTEX,{"disambiguationData":[OD(0.0)],"derivedFrom":[subQ1,subQ0]})])]});}
            var Q21;
            {var subQ0=sQuery(id+"F0.wireOp",EDGE,"E36");var subQ1=sQuery(id+"F0.wireOp",EDGE,"E2");Q21=makeQuery(id+"F1.opExtrude","SWEPT_EDGE",EDGE,{"disambiguationData":[OSD([subQ1,subQ0]),TDD([makeQuery(id+"F0.imprint","INTERSECT",VERTEX,{"disambiguationData":[OD(0.0)],"derivedFrom":[subQ1,subQ0]})])]});}
            var Q22;
            {var subQ0=sQuery(id+"F0.wireOp",EDGE,"E38");var subQ1=sQuery(id+"F0.wireOp",EDGE,"E8");Q22=makeQuery(id+"F1.opExtrude","SWEPT_EDGE",EDGE,{"disambiguationData":[OSD([subQ1,subQ0]),TDD([makeQuery(id+"F0.imprint","INTERSECT",VERTEX,{"disambiguationData":[OD(0.0)],"derivedFrom":[subQ1,subQ0]})])]});}
            var Q23;
            {var subQ0=sQuery(id+"F0.wireOp",EDGE,"E38");var subQ1=sQuery(id+"F0.wireOp",EDGE,"E4");Q23=makeQuery(id+"F1.opExtrude","SWEPT_EDGE",EDGE,{"disambiguationData":[OSD([subQ1,subQ0]),TDD([makeQuery(id+"F0.imprint","INTERSECT",VERTEX,{"disambiguationData":[OD(0.0)],"derivedFrom":[subQ1,subQ0]})])]});}
            var Q24;
            {var subQ0=sQuery(id+"F0.wireOp",EDGE,"E37");var subQ1=sQuery(id+"F0.wireOp",EDGE,"E8");Q24=makeQuery(id+"F1.opExtrude","SWEPT_EDGE",EDGE,{"disambiguationData":[OSD([subQ1,subQ0]),TDD([makeQuery(id+"F0.imprint","INTERSECT",VERTEX,{"disambiguationData":[OD(1.0)],"derivedFrom":[subQ1,subQ0]})])]});}
            var Q25;
            {var subQ0=sQuery(id+"F0.wireOp",EDGE,"E37");var subQ1=sQuery(id+"F0.wireOp",EDGE,"E3");Q25=makeQuery(id+"F1.opExtrude","SWEPT_EDGE",EDGE,{"disambiguationData":[OSD([subQ1,subQ0]),TDD([makeQuery(id+"F0.imprint","INTERSECT",VERTEX,{"disambiguationData":[OD(0.0)],"derivedFrom":[subQ1,subQ0]})])]});}
            var Q26;
            {var subQ0=sQuery(id+"F0.wireOp",EDGE,"E35");var subQ1=sQuery(id+"F0.wireOp",EDGE,"E8");Q26=makeQuery(id+"F1.opExtrude","SWEPT_EDGE",EDGE,{"disambiguationData":[OSD([subQ1,subQ0]),TDD([makeQuery(id+"F0.imprint","INTERSECT",VERTEX,{"disambiguationData":[OD(1.0)],"derivedFrom":[subQ1,subQ0]})])]});}
            var Q27;
            {var subQ0=sQuery(id+"F0.wireOp",EDGE,"E35");var subQ1=sQuery(id+"F0.wireOp",EDGE,"E1");Q27=makeQuery(id+"F1.opExtrude","SWEPT_EDGE",EDGE,{"disambiguationData":[OSD([subQ1,subQ0]),TDD([makeQuery(id+"F0.imprint","INTERSECT",VERTEX,{"disambiguationData":[OD(0.0)],"derivedFrom":[subQ1,subQ0]})])]});}
            var Q28;
            {var subQ0=sQuery(id+"F0.wireOp",EDGE,"E34");var subQ1=sQuery(id+"F0.wireOp",EDGE,"E8");Q28=makeQuery(id+"F1.opExtrude","SWEPT_EDGE",EDGE,{"disambiguationData":[OSD([subQ1,subQ0]),TDD([makeQuery(id+"F0.imprint","INTERSECT",VERTEX,{"disambiguationData":[OD(1.0)],"derivedFrom":[subQ1,subQ0]})])]});}
            var Q29;
            {var subQ0=sQuery(id+"F0.wireOp",EDGE,"E34");var subQ1=sQuery(id+"F0.wireOp",EDGE,"E1");Q29=makeQuery(id+"F1.opExtrude","SWEPT_EDGE",EDGE,{"disambiguationData":[OSD([subQ1,subQ0]),TDD([makeQuery(id+"F0.imprint","INTERSECT",VERTEX,{"disambiguationData":[OD(0.0)],"derivedFrom":[subQ1,subQ0]})])]});}
            var Q30;
            {var subQ0=sQuery(id+"F0.wireOp",EDGE,"E32");var subQ1=sQuery(id+"F0.wireOp",EDGE,"E8");Q30=makeQuery(id+"F1.opExtrude","SWEPT_EDGE",EDGE,{"disambiguationData":[OSD([subQ1,subQ0]),TDD([makeQuery(id+"F0.imprint","INTERSECT",VERTEX,{"disambiguationData":[OD(1.0)],"derivedFrom":[subQ1,subQ0]})])]});}
            var Q31;
            {var subQ0=sQuery(id+"F0.wireOp",EDGE,"E32");var subQ1=sQuery(id+"F0.wireOp",EDGE,"E3");Q31=makeQuery(id+"F1.opExtrude","SWEPT_EDGE",EDGE,{"disambiguationData":[OSD([subQ1,subQ0]),TDD([makeQuery(id+"F0.imprint","INTERSECT",VERTEX,{"disambiguationData":[OD(0.0)],"derivedFrom":[subQ1,subQ0]})])]});}
            fillet(context, id + "F2", {"entities" : qUnion([Q0, Q1, Q2, Q3, Q4, Q5, Q6, Q7, Q8, Q9, Q10, Q11, Q12, Q13, Q14, Q15, Q16, Q17, Q18, Q19, Q20, Q21, Q22, Q23, Q24, Q25, Q26, Q27, Q28, Q29, Q30, Q31]), "radius" : 3.8 * mm, "tangentPropagation" : true, "allowEdgeOverflow" : false});
        }
        {
            var Q0;
            {var subQ0=sQuery(id+"F0.wireOp",EDGE,"E40");var subQ1=makeQuery(id+"F0.imprint","INTERSECT",VERTEX,{"derivedFrom":[subQ0,sQuery(id+"F0.wireOp",EDGE,"E48")]});Q0=makeQuery(id+"F0.imprint","IMPRINT",FACE,{"disambiguationData":[TD([[makeQuery(id+"F0.imprint","IMPRINT",EDGE,{"disambiguationData":[TD([[subQ1,-1.0]])],"derivedFrom":subQ0}),1.0]])]});}
            var Q1;
            {var subQ0=sQuery(id+"F0.wireOp",EDGE,"E41");var subQ1=makeQuery(id+"F0.imprint","INTERSECT",VERTEX,{"derivedFrom":[subQ0,sQuery(id+"F0.wireOp",EDGE,"E46")]});Q1=makeQuery(id+"F0.imprint","IMPRINT",FACE,{"disambiguationData":[TD([[makeQuery(id+"F0.imprint","IMPRINT",EDGE,{"disambiguationData":[TD([[subQ1,-1.0]])],"derivedFrom":subQ0}),1.0]])]});}
            extrude(context, id + "F3", {"entities" : qUnion([Q0, Q1]), "operationType" : NewBodyOperationType.ADD, "depth" : 31.75 * mm, "offsetDistance" : 25.4 * mm});
        }
        {
            var Q0;
            Q0=makeQuery(id+"F1.opExtrude","CAP_FACE",FACE,{"disambiguationData":[OSD([sQuery(id+"F0.wireOp",EDGE,"E0"),sQuery(id+"F0.wireOp",EDGE,"E1"),sQuery(id+"F0.wireOp",EDGE,"E2"),sQuery(id+"F0.wireOp",EDGE,"E3"),sQuery(id+"F0.wireOp",EDGE,"E4"),sQuery(id+"F0.wireOp",EDGE,"E6"),sQuery(id+"F0.wireOp",EDGE,"E8"),sQuery(id+"F0.wireOp",EDGE,"E10"),sQuery(id+"F0.wireOp",EDGE,"E12"),sQuery(id+"F0.wireOp",EDGE,"E14"),sQuery(id+"F0.wireOp",EDGE,"E31"),sQuery(id+"F0.wireOp",EDGE,"E32"),sQuery(id+"F0.wireOp",EDGE,"E33"),sQuery(id+"F0.wireOp",EDGE,"E34"),sQuery(id+"F0.wireOp",EDGE,"E35"),sQuery(id+"F0.wireOp",EDGE,"E36"),sQuery(id+"F0.wireOp",EDGE,"E37"),sQuery(id+"F0.wireOp",EDGE,"E38"),sQuery(id+"F0.wireOp",EDGE,"E39"),sQuery(id+"F0.wireOp",EDGE,"E40"),sQuery(id+"F0.wireOp",EDGE,"E41"),sQuery(id+"F0.wireOp",EDGE,"E46"),sQuery(id+"F0.wireOp",EDGE,"E47"),sQuery(id+"F0.wireOp",EDGE,"E48"),sQuery(id+"F0.wireOp",EDGE,"E49")])],"isStart":false});
            var sketch = newSketch(context, id + "F4", { "sketchPlane" : qUnion([Q0])});
            skLineSegment(sketch, "E50.bottom", {"start": v(-47.5, 93.98) * mm, "end": v(80.54, 93.98) * mm});
            skLineSegment(sketch, "E50.top", {"start": v(-47.5, 106.43) * mm, "end": v(80.54, 106.43) * mm});
            skLineSegment(sketch, "E50.left", {"start": v(-47.5, 93.98) * mm, "end": v(-47.5, 106.43) * mm});
            skLineSegment(sketch, "E50.right", {"start": v(80.54, 93.98) * mm, "end": v(80.54, 106.43) * mm});
            skLineSegment(sketch, "E51.bottom", {"start": v(-53.2, -93.98) * mm, "end": v(65.32, -93.98) * mm});
            skLineSegment(sketch, "E51.top", {"start": v(-53.2, -109.2) * mm, "end": v(65.32, -109.2) * mm});
            skLineSegment(sketch, "E51.left", {"start": v(-53.2, -93.98) * mm, "end": v(-53.2, -109.2) * mm});
            skLineSegment(sketch, "E51.right", {"start": v(65.32, -93.98) * mm, "end": v(65.32, -109.2) * mm});
            skSolve(sketch);
        }
        {
            var Q0;
            Q0=makeQuery(id+"F4.imprint","IMPRINT",FACE,{"disambiguationData":[TD([[makeQuery(id+"F4.imprint","IMPRINT",EDGE,{"derivedFrom":sQuery(id+"F4.wireOp",EDGE,"E50.top")}),-1.0]])]});
            var Q1;
            {var subQ0=sQuery(id+"F4.wireOp",EDGE,"E50.bottom");var subQ1=sQuery(id+"F0.wireOp",EDGE,"E0");var subQ2=makeQuery(id+"F1.opExtrude","CAP_EDGE",EDGE,{"disambiguationData":[OSD([subQ1]),TDD([makeQuery(id+"F0.imprint","IMPRINT",EDGE,{"disambiguationData":[TD([[makeQuery(id+"F0.imprint","INTERSECT",VERTEX,{"derivedFrom":[subQ1,sQuery(id+"F0.wireOp",EDGE,"E46")]}),-1.0]])],"derivedFrom":subQ1})])],"isStart":false});var subQ3=makeQuery(id+"F4.imprint","INTERSECT",VERTEX,{"disambiguationData":[OD(0.0)],"derivedFrom":[subQ2,subQ0]});Q1=makeQuery(id+"F4.imprint","IMPRINT",FACE,{"disambiguationData":[TD([[makeQuery(id+"F4.imprint","IMPRINT",EDGE,{"disambiguationData":[TD([[subQ3,-1.0]])],"derivedFrom":subQ0}),1.0]])]});}
            var Q2;
            {var subQ0=sQuery(id+"F4.wireOp",EDGE,"E51.bottom");var subQ1=sQuery(id+"F0.wireOp",EDGE,"E12");var subQ2=sQuery(id+"F0.wireOp",EDGE,"E0");var subQ3=makeQuery(id+"F0.imprint","INTERSECT",VERTEX,{"disambiguationData":[OD(1.0)],"derivedFrom":[subQ2,subQ1]});var subQ4=makeQuery(id+"F1.opExtrude","CAP_EDGE",EDGE,{"disambiguationData":[OSD([subQ2]),TDD([makeQuery(id+"F0.imprint","IMPRINT",EDGE,{"disambiguationData":[TD([[makeQuery(id+"F0.imprint","INTERSECT",VERTEX,{"disambiguationData":[OD(0.0)],"derivedFrom":[subQ2,subQ1]}),-1.0]])],"derivedFrom":subQ2}),makeQuery(id+"F0.imprint","IMPRINT",EDGE,{"disambiguationData":[TD([[subQ3,-1.0]])],"derivedFrom":subQ2})])],"isStart":false});var subQ5=makeQuery(id+"F4.imprint","INTERSECT",VERTEX,{"disambiguationData":[OD(0.0)],"derivedFrom":[subQ4,subQ0]});Q2=makeQuery(id+"F4.imprint","IMPRINT",FACE,{"disambiguationData":[TD([[makeQuery(id+"F4.imprint","IMPRINT",EDGE,{"disambiguationData":[TD([[subQ5,-1.0]])],"derivedFrom":subQ0}),-1.0]])]});}
            var Q3;
            Q3=makeQuery(id+"F4.imprint","IMPRINT",FACE,{"disambiguationData":[TD([[makeQuery(id+"F4.imprint","IMPRINT",EDGE,{"derivedFrom":sQuery(id+"F4.wireOp",EDGE,"E51.top")}),1.0]])]});
            extrude(context, id + "F5", {"entities" : qUnion([Q0, Q1, Q2, Q3]), "operationType" : NewBodyOperationType.REMOVE, "endBound" : BoundingType.SYMMETRIC, "depth" : 25.4 * mm, "offsetDistance" : 25.4 * mm});
        }
        {
            var Q0;
            Q0=qCreatedBy(makeId("Top.planeOp"),FACE);
            var sketch = newSketch(context, id + "F6", { "sketchPlane" : qUnion([Q0])});
            skCircle(sketch, "E52", {"center": v(0, 0) * mm, "radius": 101.6 * mm});
            skCircle(sketch, "E53", {"center": v(0, 0) * mm, "radius": 95.25 * mm});
            skPoint(sketch, "E54.0", {"position": v(123.54, 38.1) * mm});
            skPoint(sketch, "E55.0", {"position": v(123.54, -38.8) * mm});
            skPoint(sketch, "E56.0", {"position": v(-129.33, -38.8) * mm});
            skLineSegment(sketch, "E57.bottom", {"start": v(123.54, 38.1) * mm, "end": v(-129.33, 38.1) * mm});
            skLineSegment(sketch, "E57.top", {"start": v(123.54, -38.8) * mm, "end": v(-129.33, -38.8) * mm});
            skLineSegment(sketch, "E57.left", {"start": v(123.54, 38.1) * mm, "end": v(123.54, -38.8) * mm});
            skLineSegment(sketch, "E57.right", {"start": v(-129.33, 38.1) * mm, "end": v(-129.33, -38.8) * mm});
            skSolve(sketch);
        }
        {
            var Q0;
            {var subQ0=sQuery(id+"F6.wireOp",EDGE,"E57.bottom");var subQ1=sQuery(id+"F6.wireOp",EDGE,"E52");var subQ2=makeQuery(id+"F6.imprint","INTERSECT",VERTEX,{"disambiguationData":[OD(1.0)],"derivedFrom":[subQ1,subQ0]});Q0=makeQuery(id+"F6.imprint","IMPRINT",FACE,{"disambiguationData":[TD([[makeQuery(id+"F6.imprint","IMPRINT",EDGE,{"disambiguationData":[TD([[subQ2,1.0]])],"derivedFrom":subQ1}),1.0]])]});}
            var Q1;
            {var subQ0=sQuery(id+"F6.wireOp",EDGE,"E57.bottom");var subQ1=sQuery(id+"F6.wireOp",EDGE,"E52");var subQ2=makeQuery(id+"F6.imprint","INTERSECT",VERTEX,{"disambiguationData":[OD(0.0)],"derivedFrom":[subQ1,subQ0]});Q1=makeQuery(id+"F6.imprint","IMPRINT",FACE,{"disambiguationData":[TD([[makeQuery(id+"F6.imprint","IMPRINT",EDGE,{"disambiguationData":[TD([[subQ2,-1.0]])],"derivedFrom":subQ1}),1.0]])]});}
            extrude(context, id + "F7", {"entities" : qUnion([Q0, Q1]), "operationType" : NewBodyOperationType.ADD, "depth" : 1.52 * mm, "offsetDistance" : 25.4 * mm});
        }
    });
